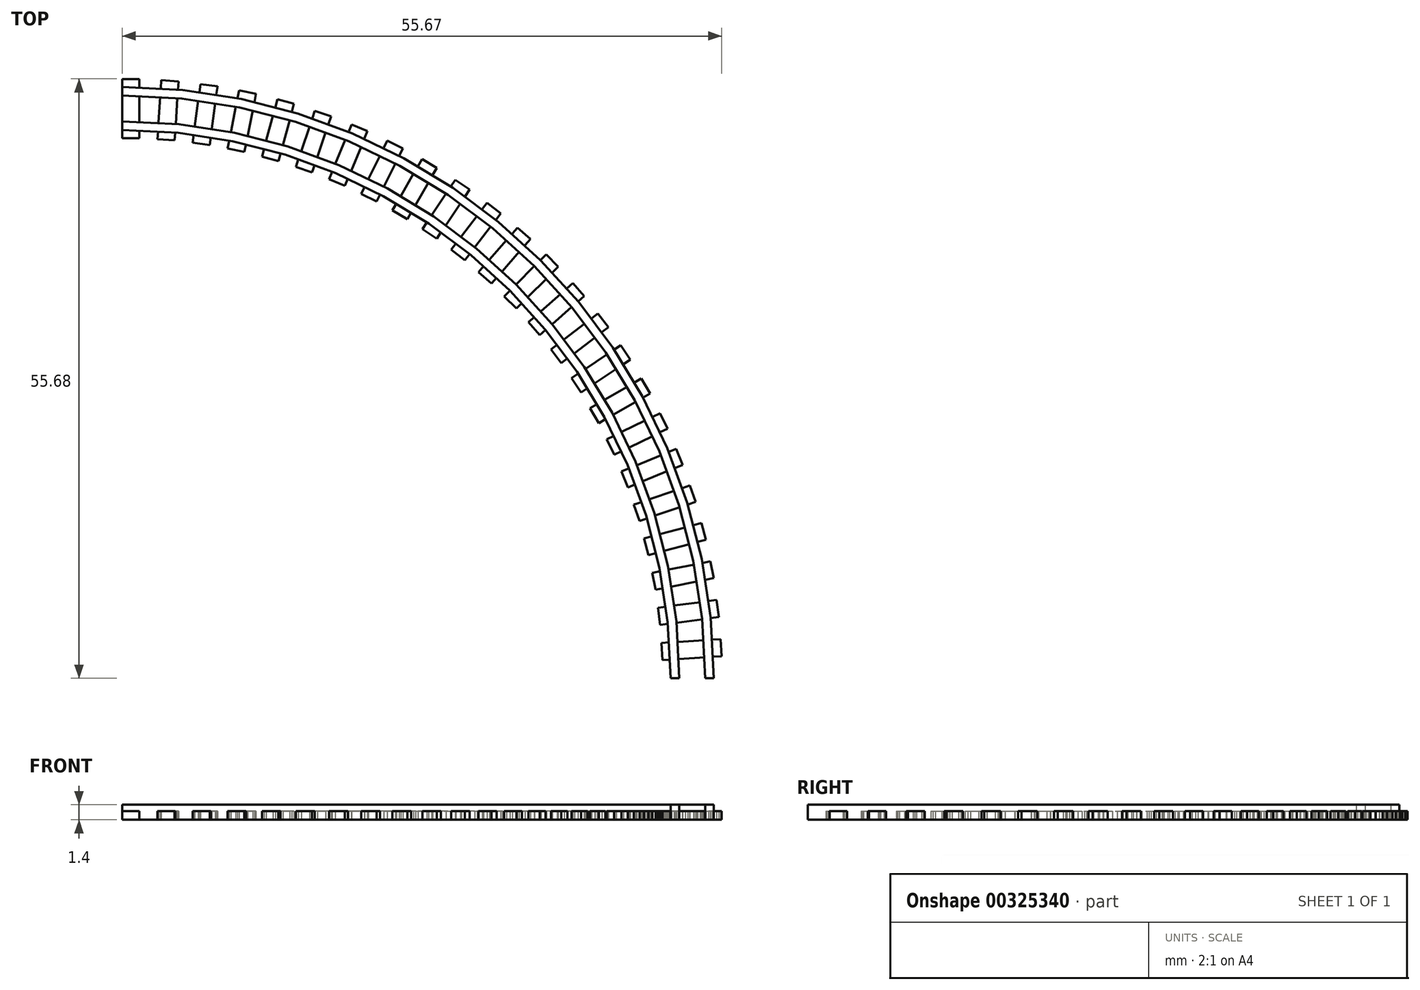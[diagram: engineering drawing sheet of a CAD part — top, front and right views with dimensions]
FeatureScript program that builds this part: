
annotation { "Feature Type Name" : "Feature", "Feature Type Description" : "" }
export const myFeature = defineFeature(function(context is Context, id is Id, definition is map)
    precondition{}
    {
        {
            var Q0;
            Q0=qCreatedBy(makeId("Top.planeOp"),FACE);
            var sketch = newSketch(context, id + "F0", { "sketchPlane" : qUnion([Q0])});
            skArc(sketch, "E0", {"start": v(50.93, 0) * mm, "mid": v(36.01, 36.01) * mm, "end": v(0, 50.93) * mm});
            skLineSegment(sketch, "E1.bottom", {"start": v(1.6, 50.18) * mm, "end": v(0, 50.18) * mm});
            skLineSegment(sketch, "E1.top", {"start": v(1.6, 55.68) * mm, "end": v(0, 55.68) * mm});
            skLineSegment(sketch, "E1.left", {"start": v(1.6, 50.18) * mm, "end": v(1.6, 55.68) * mm});
            skLineSegment(sketch, "E1.right", {"start": v(0, 50.18) * mm, "end": v(0, 55.68) * mm});
            skPoint(sketch, "E1.middle", {"position": v(0.8, 52.93) * mm});
            skLineSegment(sketch, "E2.1.0", {"start": v(4.88, 49.97) * mm, "end": v(5.24, 55.46) * mm});
            skLineSegment(sketch, "E2.1.1", {"start": v(5.24, 55.46) * mm, "end": v(3.64, 55.56) * mm});
            skLineSegment(sketch, "E2.1.2", {"start": v(3.28, 50.07) * mm, "end": v(3.64, 55.56) * mm});
            skLineSegment(sketch, "E2.1.3", {"start": v(4.88, 49.97) * mm, "end": v(3.28, 50.07) * mm});
            skLineSegment(sketch, "E2.2.0", {"start": v(8.14, 49.54) * mm, "end": v(8.85, 55) * mm});
            skLineSegment(sketch, "E2.2.1", {"start": v(8.85, 55) * mm, "end": v(7.27, 55.2) * mm});
            skLineSegment(sketch, "E2.2.2", {"start": v(6.55, 49.75) * mm, "end": v(7.27, 55.2) * mm});
            skLineSegment(sketch, "E2.2.3", {"start": v(8.14, 49.54) * mm, "end": v(6.55, 49.75) * mm});
            skLineSegment(sketch, "E2.3.0", {"start": v(11.36, 48.9) * mm, "end": v(12.43, 54.3) * mm});
            skLineSegment(sketch, "E2.3.1", {"start": v(12.43, 54.3) * mm, "end": v(10.86, 54.6) * mm});
            skLineSegment(sketch, "E2.3.2", {"start": v(9.79, 49.22) * mm, "end": v(10.86, 54.6) * mm});
            skLineSegment(sketch, "E2.3.3", {"start": v(11.36, 48.9) * mm, "end": v(9.79, 49.22) * mm});
            skLineSegment(sketch, "E2.4.0", {"start": v(14.53, 48.06) * mm, "end": v(15.96, 53.37) * mm});
            skLineSegment(sketch, "E2.4.1", {"start": v(15.96, 53.37) * mm, "end": v(14.41, 53.78) * mm});
            skLineSegment(sketch, "E2.4.2", {"start": v(12.99, 48.47) * mm, "end": v(14.41, 53.78) * mm});
            skLineSegment(sketch, "E2.4.3", {"start": v(14.53, 48.06) * mm, "end": v(12.99, 48.47) * mm});
            skLineSegment(sketch, "E2.5.0", {"start": v(17.64, 47) * mm, "end": v(19.41, 52.21) * mm});
            skLineSegment(sketch, "E2.5.1", {"start": v(19.41, 52.21) * mm, "end": v(17.9, 52.72) * mm});
            skLineSegment(sketch, "E2.5.2", {"start": v(16.13, 47.52) * mm, "end": v(17.9, 52.72) * mm});
            skLineSegment(sketch, "E2.5.3", {"start": v(17.64, 47) * mm, "end": v(16.13, 47.52) * mm});
            skLineSegment(sketch, "E2.6.0", {"start": v(20.68, 45.75) * mm, "end": v(22.79, 50.83) * mm});
            skLineSegment(sketch, "E2.6.1", {"start": v(22.79, 50.83) * mm, "end": v(21.3, 51.44) * mm});
            skLineSegment(sketch, "E2.6.2", {"start": v(19.2, 46.36) * mm, "end": v(21.3, 51.44) * mm});
            skLineSegment(sketch, "E2.6.3", {"start": v(20.68, 45.75) * mm, "end": v(19.2, 46.36) * mm});
            skLineSegment(sketch, "E2.7.0", {"start": v(23.63, 44.3) * mm, "end": v(26.06, 49.23) * mm});
            skLineSegment(sketch, "E2.7.1", {"start": v(26.06, 49.23) * mm, "end": v(24.63, 49.94) * mm});
            skLineSegment(sketch, "E2.7.2", {"start": v(22.2, 45) * mm, "end": v(24.63, 49.94) * mm});
            skLineSegment(sketch, "E2.7.3", {"start": v(23.63, 44.3) * mm, "end": v(22.2, 45) * mm});
            skLineSegment(sketch, "E2.8.0", {"start": v(26.48, 42.66) * mm, "end": v(29.23, 47.42) * mm});
            skLineSegment(sketch, "E2.8.1", {"start": v(29.23, 47.42) * mm, "end": v(27.84, 48.22) * mm});
            skLineSegment(sketch, "E2.8.2", {"start": v(25.09, 43.46) * mm, "end": v(27.84, 48.22) * mm});
            skLineSegment(sketch, "E2.8.3", {"start": v(26.48, 42.66) * mm, "end": v(25.09, 43.46) * mm});
            skLineSegment(sketch, "E2.9.0", {"start": v(29.2, 40.83) * mm, "end": v(32.26, 45.4) * mm});
            skLineSegment(sketch, "E2.9.1", {"start": v(32.26, 45.4) * mm, "end": v(30.93, 46.3) * mm});
            skLineSegment(sketch, "E2.9.2", {"start": v(27.88, 41.72) * mm, "end": v(30.93, 46.3) * mm});
            skLineSegment(sketch, "E2.9.3", {"start": v(29.2, 40.83) * mm, "end": v(27.88, 41.72) * mm});
            skLineSegment(sketch, "E2.10.0", {"start": v(31.82, 38.84) * mm, "end": v(35.16, 43.2) * mm});
            skLineSegment(sketch, "E2.10.1", {"start": v(35.16, 43.2) * mm, "end": v(33.9, 44.17) * mm});
            skLineSegment(sketch, "E2.10.2", {"start": v(30.55, 39.81) * mm, "end": v(33.9, 44.17) * mm});
            skLineSegment(sketch, "E2.10.3", {"start": v(31.82, 38.84) * mm, "end": v(30.55, 39.81) * mm});
            skLineSegment(sketch, "E2.11.0", {"start": v(34.29, 36.67) * mm, "end": v(37.92, 40.8) * mm});
            skLineSegment(sketch, "E2.11.1", {"start": v(37.92, 40.8) * mm, "end": v(36.71, 41.86) * mm});
            skLineSegment(sketch, "E2.11.2", {"start": v(33.09, 37.73) * mm, "end": v(36.71, 41.86) * mm});
            skLineSegment(sketch, "E2.11.3", {"start": v(34.29, 36.67) * mm, "end": v(33.09, 37.73) * mm});
            skLineSegment(sketch, "E2.12.0", {"start": v(36.61, 34.35) * mm, "end": v(40.5, 38.24) * mm});
            skLineSegment(sketch, "E2.12.1", {"start": v(40.5, 38.24) * mm, "end": v(39.37, 39.37) * mm});
            skLineSegment(sketch, "E2.12.2", {"start": v(35.48, 35.48) * mm, "end": v(39.37, 39.37) * mm});
            skLineSegment(sketch, "E2.12.3", {"start": v(36.61, 34.35) * mm, "end": v(35.48, 35.48) * mm});
            skLineSegment(sketch, "E2.13.0", {"start": v(38.78, 31.88) * mm, "end": v(42.92, 35.5) * mm});
            skLineSegment(sketch, "E2.13.1", {"start": v(42.92, 35.5) * mm, "end": v(41.86, 36.71) * mm});
            skLineSegment(sketch, "E2.13.2", {"start": v(37.73, 33.09) * mm, "end": v(41.86, 36.71) * mm});
            skLineSegment(sketch, "E2.13.3", {"start": v(38.78, 31.88) * mm, "end": v(37.73, 33.09) * mm});
            skLineSegment(sketch, "E2.14.0", {"start": v(40.78, 29.28) * mm, "end": v(45.15, 32.63) * mm});
            skLineSegment(sketch, "E2.14.1", {"start": v(45.15, 32.63) * mm, "end": v(44.17, 33.9) * mm});
            skLineSegment(sketch, "E2.14.2", {"start": v(39.81, 30.55) * mm, "end": v(44.17, 33.9) * mm});
            skLineSegment(sketch, "E2.14.3", {"start": v(40.78, 29.28) * mm, "end": v(39.81, 30.55) * mm});
            skLineSegment(sketch, "E2.15.0", {"start": v(42.61, 26.55) * mm, "end": v(47.18, 29.6) * mm});
            skLineSegment(sketch, "E2.15.1", {"start": v(47.18, 29.6) * mm, "end": v(46.3, 30.93) * mm});
            skLineSegment(sketch, "E2.15.2", {"start": v(41.72, 27.88) * mm, "end": v(46.3, 30.93) * mm});
            skLineSegment(sketch, "E2.15.3", {"start": v(42.61, 26.55) * mm, "end": v(41.72, 27.88) * mm});
            skLineSegment(sketch, "E2.16.0", {"start": v(44.26, 23.7) * mm, "end": v(49.02, 26.45) * mm});
            skLineSegment(sketch, "E2.16.1", {"start": v(49.02, 26.45) * mm, "end": v(48.22, 27.84) * mm});
            skLineSegment(sketch, "E2.16.2", {"start": v(43.46, 25.09) * mm, "end": v(48.22, 27.84) * mm});
            skLineSegment(sketch, "E2.16.3", {"start": v(44.26, 23.7) * mm, "end": v(43.46, 25.09) * mm});
            skLineSegment(sketch, "E2.17.0", {"start": v(45.71, 20.76) * mm, "end": v(50.65, 23.2) * mm});
            skLineSegment(sketch, "E2.17.1", {"start": v(50.65, 23.2) * mm, "end": v(49.94, 24.63) * mm});
            skLineSegment(sketch, "E2.17.2", {"start": v(45, 22.2) * mm, "end": v(49.94, 24.63) * mm});
            skLineSegment(sketch, "E2.17.3", {"start": v(45.71, 20.76) * mm, "end": v(45, 22.2) * mm});
            skLineSegment(sketch, "E2.18.0", {"start": v(46.97, 17.72) * mm, "end": v(52.05, 19.83) * mm});
            skLineSegment(sketch, "E2.18.1", {"start": v(52.05, 19.83) * mm, "end": v(51.44, 21.3) * mm});
            skLineSegment(sketch, "E2.18.2", {"start": v(46.36, 19.2) * mm, "end": v(51.44, 21.3) * mm});
            skLineSegment(sketch, "E2.18.3", {"start": v(46.97, 17.72) * mm, "end": v(46.36, 19.2) * mm});
            skLineSegment(sketch, "E2.19.0", {"start": v(48.03, 14.61) * mm, "end": v(53.24, 16.38) * mm});
            skLineSegment(sketch, "E2.19.1", {"start": v(53.24, 16.38) * mm, "end": v(52.72, 17.9) * mm});
            skLineSegment(sketch, "E2.19.2", {"start": v(47.52, 16.13) * mm, "end": v(52.72, 17.9) * mm});
            skLineSegment(sketch, "E2.19.3", {"start": v(48.03, 14.61) * mm, "end": v(47.52, 16.13) * mm});
            skLineSegment(sketch, "E2.20.0", {"start": v(48.88, 11.44) * mm, "end": v(54.2, 12.87) * mm});
            skLineSegment(sketch, "E2.20.1", {"start": v(54.2, 12.87) * mm, "end": v(53.78, 14.41) * mm});
            skLineSegment(sketch, "E2.20.2", {"start": v(48.47, 12.99) * mm, "end": v(53.78, 14.41) * mm});
            skLineSegment(sketch, "E2.20.3", {"start": v(48.88, 11.44) * mm, "end": v(48.47, 12.99) * mm});
            skLineSegment(sketch, "E2.21.0", {"start": v(49.53, 8.22) * mm, "end": v(54.92, 9.3) * mm});
            skLineSegment(sketch, "E2.21.1", {"start": v(54.92, 9.3) * mm, "end": v(54.6, 10.86) * mm});
            skLineSegment(sketch, "E2.21.2", {"start": v(49.22, 9.79) * mm, "end": v(54.6, 10.86) * mm});
            skLineSegment(sketch, "E2.21.3", {"start": v(49.53, 8.22) * mm, "end": v(49.22, 9.79) * mm});
            skLineSegment(sketch, "E2.22.0", {"start": v(49.96, 4.96) * mm, "end": v(55.41, 5.68) * mm});
            skLineSegment(sketch, "E2.22.1", {"start": v(55.41, 5.68) * mm, "end": v(55.2, 7.27) * mm});
            skLineSegment(sketch, "E2.22.2", {"start": v(49.75, 6.55) * mm, "end": v(55.2, 7.27) * mm});
            skLineSegment(sketch, "E2.22.3", {"start": v(49.96, 4.96) * mm, "end": v(49.75, 6.55) * mm});
            skLineSegment(sketch, "E2.23.0", {"start": v(50.18, 1.69) * mm, "end": v(55.67, 2.05) * mm});
            skLineSegment(sketch, "E2.23.1", {"start": v(55.67, 2.05) * mm, "end": v(55.56, 3.64) * mm});
            skLineSegment(sketch, "E2.23.2", {"start": v(50.07, 3.28) * mm, "end": v(55.56, 3.64) * mm});
            skLineSegment(sketch, "E2.23.3", {"start": v(50.18, 1.69) * mm, "end": v(50.07, 3.28) * mm});
            skLineSegment(sketch, "E3.0.24.0", {"start": v(50.18, -1.6) * mm, "end": v(55.68, -1.6) * mm});
            skLineSegment(sketch, "E3.3.24.0", {"start": v(55.68, -1.6) * mm, "end": v(55.68, 0) * mm});
            skLineSegment(sketch, "E3.6.24.0", {"start": v(50.18, 0) * mm, "end": v(55.68, 0) * mm});
            skLineSegment(sketch, "E3.9.24.0", {"start": v(50.18, -1.6) * mm, "end": v(50.18, 0) * mm});
            skArc(sketch, "E4", {"start": v(51.74, 0) * mm, "mid": v(36.59, 36.59) * mm, "end": v(0, 51.74) * mm});
            skArc(sketch, "E5", {"start": v(54.14, 0) * mm, "mid": v(38.28, 38.28) * mm, "end": v(0, 54.14) * mm});
            skArc(sketch, "E6", {"start": v(54.94, 0) * mm, "mid": v(38.85, 38.85) * mm, "end": v(0, 54.94) * mm});
            skSolve(sketch);
        }
        {
            var Q0;
            {var subQ0=sQuery(id+"F0.wireOp",EDGE,"E4");var subQ1=sQuery(id+"F0.wireOp",EDGE,"E2.5.0");var subQ2=makeQuery(id+"F0.imprint","INTERSECT",VERTEX,{"derivedFrom":[subQ1,subQ0]});Q0=makeQuery(id+"F0.imprint","IMPRINT",FACE,{"disambiguationData":[TD([[makeQuery(id+"F0.imprint","IMPRINT",EDGE,{"disambiguationData":[TD([[subQ2,-1.0]])],"derivedFrom":subQ1}),1.0]])]});}
            var Q1;
            {var subQ0=sQuery(id+"F0.wireOp",EDGE,"E2.3.0");var subQ1=sQuery(id+"F0.wireOp",EDGE,"E0");var subQ2=makeQuery(id+"F0.imprint","INTERSECT",VERTEX,{"derivedFrom":[subQ1,subQ0]});Q1=makeQuery(id+"F0.imprint","IMPRINT",FACE,{"disambiguationData":[TD([[makeQuery(id+"F0.imprint","IMPRINT",EDGE,{"disambiguationData":[TD([[subQ2,-1.0]])],"derivedFrom":subQ1}),-1.0]])]});}
            var Q2;
            {var subQ0=sQuery(id+"F0.wireOp",EDGE,"E4");var subQ1=sQuery(id+"F0.wireOp",EDGE,"E2.21.0");var subQ2=makeQuery(id+"F0.imprint","INTERSECT",VERTEX,{"derivedFrom":[subQ1,subQ0]});Q2=makeQuery(id+"F0.imprint","IMPRINT",FACE,{"disambiguationData":[TD([[makeQuery(id+"F0.imprint","IMPRINT",EDGE,{"disambiguationData":[TD([[subQ2,-1.0]])],"derivedFrom":subQ1}),1.0]])]});}
            var Q3;
            {var subQ0=sQuery(id+"F0.wireOp",EDGE,"E4");var subQ1=sQuery(id+"F0.wireOp",EDGE,"E2.3.0");var subQ2=makeQuery(id+"F0.imprint","INTERSECT",VERTEX,{"derivedFrom":[subQ1,subQ0]});Q3=makeQuery(id+"F0.imprint","IMPRINT",FACE,{"disambiguationData":[TD([[makeQuery(id+"F0.imprint","IMPRINT",EDGE,{"disambiguationData":[TD([[subQ2,-1.0]])],"derivedFrom":subQ1}),1.0]])]});}
            var Q4;
            {var subQ0=sQuery(id+"F0.wireOp",EDGE,"E4");var subQ1=sQuery(id+"F0.wireOp",EDGE,"E2.19.0");var subQ2=makeQuery(id+"F0.imprint","INTERSECT",VERTEX,{"derivedFrom":[subQ1,subQ0]});Q4=makeQuery(id+"F0.imprint","IMPRINT",FACE,{"disambiguationData":[TD([[makeQuery(id+"F0.imprint","IMPRINT",EDGE,{"disambiguationData":[TD([[subQ2,-1.0]])],"derivedFrom":subQ1}),1.0]])]});}
            var Q5;
            {var subQ0=sQuery(id+"F0.wireOp",EDGE,"E4");var subQ1=sQuery(id+"F0.wireOp",EDGE,"E2.16.0");var subQ2=makeQuery(id+"F0.imprint","INTERSECT",VERTEX,{"derivedFrom":[subQ1,subQ0]});Q5=makeQuery(id+"F0.imprint","IMPRINT",FACE,{"disambiguationData":[TD([[makeQuery(id+"F0.imprint","IMPRINT",EDGE,{"disambiguationData":[TD([[subQ2,-1.0]])],"derivedFrom":subQ1}),1.0]])]});}
            var Q6;
            {var subQ0=sQuery(id+"F0.wireOp",EDGE,"E4");var subQ1=sQuery(id+"F0.wireOp",EDGE,"E2.11.0");var subQ2=makeQuery(id+"F0.imprint","INTERSECT",VERTEX,{"derivedFrom":[subQ1,subQ0]});Q6=makeQuery(id+"F0.imprint","IMPRINT",FACE,{"disambiguationData":[TD([[makeQuery(id+"F0.imprint","IMPRINT",EDGE,{"disambiguationData":[TD([[subQ2,-1.0]])],"derivedFrom":subQ1}),1.0]])]});}
            var Q7;
            {var subQ0=sQuery(id+"F0.wireOp",EDGE,"E4");var subQ1=sQuery(id+"F0.wireOp",EDGE,"E2.22.0");var subQ2=makeQuery(id+"F0.imprint","INTERSECT",VERTEX,{"derivedFrom":[subQ1,subQ0]});Q7=makeQuery(id+"F0.imprint","IMPRINT",FACE,{"disambiguationData":[TD([[makeQuery(id+"F0.imprint","IMPRINT",EDGE,{"disambiguationData":[TD([[subQ2,-1.0]])],"derivedFrom":subQ1}),1.0]])]});}
            var Q8;
            {var subQ0=sQuery(id+"F0.wireOp",EDGE,"E4");var subQ1=sQuery(id+"F0.wireOp",EDGE,"E2.7.0");var subQ2=makeQuery(id+"F0.imprint","INTERSECT",VERTEX,{"derivedFrom":[subQ1,subQ0]});Q8=makeQuery(id+"F0.imprint","IMPRINT",FACE,{"disambiguationData":[TD([[makeQuery(id+"F0.imprint","IMPRINT",EDGE,{"disambiguationData":[TD([[subQ2,-1.0]])],"derivedFrom":subQ1}),1.0]])]});}
            var Q9;
            {var subQ0=sQuery(id+"F0.wireOp",EDGE,"E4");var subQ1=sQuery(id+"F0.wireOp",EDGE,"E2.4.0");var subQ2=makeQuery(id+"F0.imprint","INTERSECT",VERTEX,{"derivedFrom":[subQ1,subQ0]});Q9=makeQuery(id+"F0.imprint","IMPRINT",FACE,{"disambiguationData":[TD([[makeQuery(id+"F0.imprint","IMPRINT",EDGE,{"disambiguationData":[TD([[subQ2,-1.0]])],"derivedFrom":subQ1}),1.0]])]});}
            var Q10;
            {var subQ0=sQuery(id+"F0.wireOp",EDGE,"E4");var subQ1=sQuery(id+"F0.wireOp",EDGE,"E2.1.0");var subQ2=makeQuery(id+"F0.imprint","INTERSECT",VERTEX,{"derivedFrom":[subQ1,subQ0]});Q10=makeQuery(id+"F0.imprint","IMPRINT",FACE,{"disambiguationData":[TD([[makeQuery(id+"F0.imprint","IMPRINT",EDGE,{"disambiguationData":[TD([[subQ2,-1.0]])],"derivedFrom":subQ1}),1.0]])]});}
            var Q11;
            {var subQ0=sQuery(id+"F0.wireOp",EDGE,"E4");var subQ1=sQuery(id+"F0.wireOp",EDGE,"E2.17.0");var subQ2=makeQuery(id+"F0.imprint","INTERSECT",VERTEX,{"derivedFrom":[subQ1,subQ0]});Q11=makeQuery(id+"F0.imprint","IMPRINT",FACE,{"disambiguationData":[TD([[makeQuery(id+"F0.imprint","IMPRINT",EDGE,{"disambiguationData":[TD([[subQ2,-1.0]])],"derivedFrom":subQ1}),1.0]])]});}
            var Q12;
            {var subQ0=sQuery(id+"F0.wireOp",EDGE,"E4");var subQ1=sQuery(id+"F0.wireOp",EDGE,"E2.10.0");var subQ2=makeQuery(id+"F0.imprint","INTERSECT",VERTEX,{"derivedFrom":[subQ1,subQ0]});Q12=makeQuery(id+"F0.imprint","IMPRINT",FACE,{"disambiguationData":[TD([[makeQuery(id+"F0.imprint","IMPRINT",EDGE,{"disambiguationData":[TD([[subQ2,-1.0]])],"derivedFrom":subQ1}),1.0]])]});}
            var Q13;
            {var subQ0=sQuery(id+"F0.wireOp",EDGE,"E4");var subQ1=sQuery(id+"F0.wireOp",EDGE,"E2.13.0");var subQ2=makeQuery(id+"F0.imprint","INTERSECT",VERTEX,{"derivedFrom":[subQ1,subQ0]});Q13=makeQuery(id+"F0.imprint","IMPRINT",FACE,{"disambiguationData":[TD([[makeQuery(id+"F0.imprint","IMPRINT",EDGE,{"disambiguationData":[TD([[subQ2,-1.0]])],"derivedFrom":subQ1}),1.0]])]});}
            var Q14;
            {var subQ0=sQuery(id+"F0.wireOp",EDGE,"E4");var subQ1=sQuery(id+"F0.wireOp",EDGE,"E2.8.0");var subQ2=makeQuery(id+"F0.imprint","INTERSECT",VERTEX,{"derivedFrom":[subQ1,subQ0]});Q14=makeQuery(id+"F0.imprint","IMPRINT",FACE,{"disambiguationData":[TD([[makeQuery(id+"F0.imprint","IMPRINT",EDGE,{"disambiguationData":[TD([[subQ2,-1.0]])],"derivedFrom":subQ1}),1.0]])]});}
            var Q15;
            {var subQ0=sQuery(id+"F0.wireOp",EDGE,"E4");var subQ1=sQuery(id+"F0.wireOp",EDGE,"E2.15.0");var subQ2=makeQuery(id+"F0.imprint","INTERSECT",VERTEX,{"derivedFrom":[subQ1,subQ0]});Q15=makeQuery(id+"F0.imprint","IMPRINT",FACE,{"disambiguationData":[TD([[makeQuery(id+"F0.imprint","IMPRINT",EDGE,{"disambiguationData":[TD([[subQ2,-1.0]])],"derivedFrom":subQ1}),1.0]])]});}
            var Q16;
            {var subQ0=sQuery(id+"F0.wireOp",EDGE,"E4");var subQ1=sQuery(id+"F0.wireOp",EDGE,"E2.2.0");var subQ2=makeQuery(id+"F0.imprint","INTERSECT",VERTEX,{"derivedFrom":[subQ1,subQ0]});Q16=makeQuery(id+"F0.imprint","IMPRINT",FACE,{"disambiguationData":[TD([[makeQuery(id+"F0.imprint","IMPRINT",EDGE,{"disambiguationData":[TD([[subQ2,-1.0]])],"derivedFrom":subQ1}),1.0]])]});}
            var Q17;
            {var subQ0=sQuery(id+"F0.wireOp",EDGE,"E4");var subQ1=sQuery(id+"F0.wireOp",EDGE,"E2.18.0");var subQ2=makeQuery(id+"F0.imprint","INTERSECT",VERTEX,{"derivedFrom":[subQ1,subQ0]});Q17=makeQuery(id+"F0.imprint","IMPRINT",FACE,{"disambiguationData":[TD([[makeQuery(id+"F0.imprint","IMPRINT",EDGE,{"disambiguationData":[TD([[subQ2,-1.0]])],"derivedFrom":subQ1}),1.0]])]});}
            var Q18;
            {var subQ0=sQuery(id+"F0.wireOp",EDGE,"E4");var subQ1=sQuery(id+"F0.wireOp",EDGE,"E2.20.0");var subQ2=makeQuery(id+"F0.imprint","INTERSECT",VERTEX,{"derivedFrom":[subQ1,subQ0]});Q18=makeQuery(id+"F0.imprint","IMPRINT",FACE,{"disambiguationData":[TD([[makeQuery(id+"F0.imprint","IMPRINT",EDGE,{"disambiguationData":[TD([[subQ2,-1.0]])],"derivedFrom":subQ1}),1.0]])]});}
            var Q19;
            {var subQ0=sQuery(id+"F0.wireOp",EDGE,"E4");var subQ1=sQuery(id+"F0.wireOp",EDGE,"E2.23.0");var subQ2=makeQuery(id+"F0.imprint","INTERSECT",VERTEX,{"derivedFrom":[subQ1,subQ0]});Q19=makeQuery(id+"F0.imprint","IMPRINT",FACE,{"disambiguationData":[TD([[makeQuery(id+"F0.imprint","IMPRINT",EDGE,{"disambiguationData":[TD([[subQ2,-1.0]])],"derivedFrom":subQ1}),1.0]])]});}
            var Q20;
            {var subQ0=sQuery(id+"F0.wireOp",EDGE,"E4");var subQ1=sQuery(id+"F0.wireOp",EDGE,"E2.6.0");var subQ2=makeQuery(id+"F0.imprint","INTERSECT",VERTEX,{"derivedFrom":[subQ1,subQ0]});Q20=makeQuery(id+"F0.imprint","IMPRINT",FACE,{"disambiguationData":[TD([[makeQuery(id+"F0.imprint","IMPRINT",EDGE,{"disambiguationData":[TD([[subQ2,-1.0]])],"derivedFrom":subQ1}),1.0]])]});}
            var Q21;
            {var subQ0=sQuery(id+"F0.wireOp",EDGE,"E4");var subQ1=sQuery(id+"F0.wireOp",EDGE,"E2.12.0");var subQ2=makeQuery(id+"F0.imprint","INTERSECT",VERTEX,{"derivedFrom":[subQ1,subQ0]});Q21=makeQuery(id+"F0.imprint","IMPRINT",FACE,{"disambiguationData":[TD([[makeQuery(id+"F0.imprint","IMPRINT",EDGE,{"disambiguationData":[TD([[subQ2,-1.0]])],"derivedFrom":subQ1}),1.0]])]});}
            var Q22;
            {var subQ0=sQuery(id+"F0.wireOp",EDGE,"E4");var subQ1=sQuery(id+"F0.wireOp",EDGE,"E2.9.0");var subQ2=makeQuery(id+"F0.imprint","INTERSECT",VERTEX,{"derivedFrom":[subQ1,subQ0]});Q22=makeQuery(id+"F0.imprint","IMPRINT",FACE,{"disambiguationData":[TD([[makeQuery(id+"F0.imprint","IMPRINT",EDGE,{"disambiguationData":[TD([[subQ2,-1.0]])],"derivedFrom":subQ1}),1.0]])]});}
            var Q23;
            {var subQ0=sQuery(id+"F0.wireOp",EDGE,"E4");var subQ1=sQuery(id+"F0.wireOp",EDGE,"E2.14.0");var subQ2=makeQuery(id+"F0.imprint","INTERSECT",VERTEX,{"derivedFrom":[subQ1,subQ0]});Q23=makeQuery(id+"F0.imprint","IMPRINT",FACE,{"disambiguationData":[TD([[makeQuery(id+"F0.imprint","IMPRINT",EDGE,{"disambiguationData":[TD([[subQ2,-1.0]])],"derivedFrom":subQ1}),1.0]])]});}
            var Q24;
            {var subQ0=sQuery(id+"F0.wireOp",EDGE,"E2.6.2");var subQ1=sQuery(id+"F0.wireOp",EDGE,"E0");var subQ2=makeQuery(id+"F0.imprint","INTERSECT",VERTEX,{"derivedFrom":[subQ1,subQ0]});Q24=makeQuery(id+"F0.imprint","IMPRINT",FACE,{"disambiguationData":[TD([[makeQuery(id+"F0.imprint","IMPRINT",EDGE,{"disambiguationData":[TD([[subQ2,-1.0]])],"derivedFrom":subQ1}),-1.0]])]});}
            var Q25;
            {var subQ0=sQuery(id+"F0.wireOp",EDGE,"E2.10.0");var subQ1=sQuery(id+"F0.wireOp",EDGE,"E0");var subQ2=makeQuery(id+"F0.imprint","INTERSECT",VERTEX,{"derivedFrom":[subQ1,subQ0]});Q25=makeQuery(id+"F0.imprint","IMPRINT",FACE,{"disambiguationData":[TD([[makeQuery(id+"F0.imprint","IMPRINT",EDGE,{"disambiguationData":[TD([[subQ2,-1.0]])],"derivedFrom":subQ1}),-1.0]])]});}
            var Q26;
            {var subQ0=sQuery(id+"F0.wireOp",EDGE,"E6");var subQ1=sQuery(id+"F0.wireOp",EDGE,"E2.21.0");var subQ2=makeQuery(id+"F0.imprint","INTERSECT",VERTEX,{"derivedFrom":[subQ1,subQ0]});Q26=makeQuery(id+"F0.imprint","IMPRINT",FACE,{"disambiguationData":[TD([[makeQuery(id+"F0.imprint","IMPRINT",EDGE,{"disambiguationData":[TD([[subQ2,1.0]])],"derivedFrom":subQ1}),-1.0]])]});}
            var Q27;
            {var subQ0=sQuery(id+"F0.wireOp",EDGE,"E6");var subQ1=sQuery(id+"F0.wireOp",EDGE,"E2.22.0");var subQ2=makeQuery(id+"F0.imprint","INTERSECT",VERTEX,{"derivedFrom":[subQ1,subQ0]});Q27=makeQuery(id+"F0.imprint","IMPRINT",FACE,{"disambiguationData":[TD([[makeQuery(id+"F0.imprint","IMPRINT",EDGE,{"disambiguationData":[TD([[subQ2,1.0]])],"derivedFrom":subQ1}),-1.0]])]});}
            var Q28;
            {var subQ0=sQuery(id+"F0.wireOp",EDGE,"E2.4.0");var subQ1=sQuery(id+"F0.wireOp",EDGE,"E0");var subQ2=makeQuery(id+"F0.imprint","INTERSECT",VERTEX,{"derivedFrom":[subQ1,subQ0]});Q28=makeQuery(id+"F0.imprint","IMPRINT",FACE,{"disambiguationData":[TD([[makeQuery(id+"F0.imprint","IMPRINT",EDGE,{"disambiguationData":[TD([[subQ2,-1.0]])],"derivedFrom":subQ1}),-1.0]])]});}
            var Q29;
            {var subQ0=sQuery(id+"F0.wireOp",EDGE,"E2.16.2");var subQ1=sQuery(id+"F0.wireOp",EDGE,"E0");var subQ2=makeQuery(id+"F0.imprint","INTERSECT",VERTEX,{"derivedFrom":[subQ1,subQ0]});Q29=makeQuery(id+"F0.imprint","IMPRINT",FACE,{"disambiguationData":[TD([[makeQuery(id+"F0.imprint","IMPRINT",EDGE,{"disambiguationData":[TD([[subQ2,-1.0]])],"derivedFrom":subQ1}),-1.0]])]});}
            var Q30;
            {var subQ0=sQuery(id+"F0.wireOp",EDGE,"E6");var subQ1=sQuery(id+"F0.wireOp",EDGE,"E2.13.0");var subQ2=makeQuery(id+"F0.imprint","INTERSECT",VERTEX,{"derivedFrom":[subQ1,subQ0]});Q30=makeQuery(id+"F0.imprint","IMPRINT",FACE,{"disambiguationData":[TD([[makeQuery(id+"F0.imprint","IMPRINT",EDGE,{"disambiguationData":[TD([[subQ2,1.0]])],"derivedFrom":subQ1}),-1.0]])]});}
            var Q31;
            {var subQ0=sQuery(id+"F0.wireOp",EDGE,"E6");var subQ1=sQuery(id+"F0.wireOp",EDGE,"E2.20.0");var subQ2=makeQuery(id+"F0.imprint","INTERSECT",VERTEX,{"derivedFrom":[subQ1,subQ0]});Q31=makeQuery(id+"F0.imprint","IMPRINT",FACE,{"disambiguationData":[TD([[makeQuery(id+"F0.imprint","IMPRINT",EDGE,{"disambiguationData":[TD([[subQ2,1.0]])],"derivedFrom":subQ1}),-1.0]])]});}
            var Q32;
            {var subQ0=sQuery(id+"F0.wireOp",EDGE,"E6");var subQ1=sQuery(id+"F0.wireOp",EDGE,"E2.4.0");var subQ2=makeQuery(id+"F0.imprint","INTERSECT",VERTEX,{"derivedFrom":[subQ1,subQ0]});Q32=makeQuery(id+"F0.imprint","IMPRINT",FACE,{"disambiguationData":[TD([[makeQuery(id+"F0.imprint","IMPRINT",EDGE,{"disambiguationData":[TD([[subQ2,1.0]])],"derivedFrom":subQ1}),-1.0]])]});}
            var Q33;
            {var subQ0=sQuery(id+"F0.wireOp",EDGE,"E6");var subQ1=sQuery(id+"F0.wireOp",EDGE,"E2.21.0");var subQ2=makeQuery(id+"F0.imprint","INTERSECT",VERTEX,{"derivedFrom":[subQ1,subQ0]});Q33=makeQuery(id+"F0.imprint","IMPRINT",FACE,{"disambiguationData":[TD([[makeQuery(id+"F0.imprint","IMPRINT",EDGE,{"disambiguationData":[TD([[subQ2,1.0]])],"derivedFrom":subQ1}),1.0]])]});}
            var Q34;
            {var subQ0=sQuery(id+"F0.wireOp",EDGE,"E6");var subQ1=sQuery(id+"F0.wireOp",EDGE,"E2.5.0");var subQ2=makeQuery(id+"F0.imprint","INTERSECT",VERTEX,{"derivedFrom":[subQ1,subQ0]});Q34=makeQuery(id+"F0.imprint","IMPRINT",FACE,{"disambiguationData":[TD([[makeQuery(id+"F0.imprint","IMPRINT",EDGE,{"disambiguationData":[TD([[subQ2,1.0]])],"derivedFrom":subQ1}),1.0]])]});}
            var Q35;
            {var subQ0=sQuery(id+"F0.wireOp",EDGE,"E2.4.2");var subQ1=sQuery(id+"F0.wireOp",EDGE,"E0");var subQ2=makeQuery(id+"F0.imprint","INTERSECT",VERTEX,{"derivedFrom":[subQ1,subQ0]});Q35=makeQuery(id+"F0.imprint","IMPRINT",FACE,{"disambiguationData":[TD([[makeQuery(id+"F0.imprint","IMPRINT",EDGE,{"disambiguationData":[TD([[subQ2,-1.0]])],"derivedFrom":subQ1}),-1.0]])]});}
            var Q36;
            {var subQ0=sQuery(id+"F0.wireOp",EDGE,"E6");var subQ1=sQuery(id+"F0.wireOp",EDGE,"E2.2.0");var subQ2=makeQuery(id+"F0.imprint","INTERSECT",VERTEX,{"derivedFrom":[subQ1,subQ0]});Q36=makeQuery(id+"F0.imprint","IMPRINT",FACE,{"disambiguationData":[TD([[makeQuery(id+"F0.imprint","IMPRINT",EDGE,{"disambiguationData":[TD([[subQ2,1.0]])],"derivedFrom":subQ1}),-1.0]])]});}
            var Q37;
            {var subQ0=sQuery(id+"F0.wireOp",EDGE,"E2.7.0");var subQ1=sQuery(id+"F0.wireOp",EDGE,"E0");var subQ2=makeQuery(id+"F0.imprint","INTERSECT",VERTEX,{"derivedFrom":[subQ1,subQ0]});Q37=makeQuery(id+"F0.imprint","IMPRINT",FACE,{"disambiguationData":[TD([[makeQuery(id+"F0.imprint","IMPRINT",EDGE,{"disambiguationData":[TD([[subQ2,-1.0]])],"derivedFrom":subQ1}),-1.0]])]});}
            var Q38;
            {var subQ0=sQuery(id+"F0.wireOp",EDGE,"E6");var subQ1=sQuery(id+"F0.wireOp",EDGE,"E1.left");var subQ2=makeQuery(id+"F0.imprint","INTERSECT",VERTEX,{"derivedFrom":[subQ1,subQ0]});Q38=makeQuery(id+"F0.imprint","IMPRINT",FACE,{"disambiguationData":[TD([[makeQuery(id+"F0.imprint","IMPRINT",EDGE,{"disambiguationData":[TD([[subQ2,1.0]])],"derivedFrom":subQ1}),-1.0]])]});}
            var Q39;
            {var subQ0=sQuery(id+"F0.wireOp",EDGE,"E2.10.2");var subQ1=sQuery(id+"F0.wireOp",EDGE,"E0");var subQ2=makeQuery(id+"F0.imprint","INTERSECT",VERTEX,{"derivedFrom":[subQ1,subQ0]});Q39=makeQuery(id+"F0.imprint","IMPRINT",FACE,{"disambiguationData":[TD([[makeQuery(id+"F0.imprint","IMPRINT",EDGE,{"disambiguationData":[TD([[subQ2,-1.0]])],"derivedFrom":subQ1}),-1.0]])]});}
            var Q40;
            {var subQ0=sQuery(id+"F0.wireOp",EDGE,"E2.3.2");var subQ1=sQuery(id+"F0.wireOp",EDGE,"E0");var subQ2=makeQuery(id+"F0.imprint","INTERSECT",VERTEX,{"derivedFrom":[subQ1,subQ0]});Q40=makeQuery(id+"F0.imprint","IMPRINT",FACE,{"disambiguationData":[TD([[makeQuery(id+"F0.imprint","IMPRINT",EDGE,{"disambiguationData":[TD([[subQ2,-1.0]])],"derivedFrom":subQ1}),-1.0]])]});}
            var Q41;
            {var subQ0=sQuery(id+"F0.wireOp",EDGE,"E2.19.2");var subQ1=sQuery(id+"F0.wireOp",EDGE,"E0");var subQ2=makeQuery(id+"F0.imprint","INTERSECT",VERTEX,{"derivedFrom":[subQ1,subQ0]});Q41=makeQuery(id+"F0.imprint","IMPRINT",FACE,{"disambiguationData":[TD([[makeQuery(id+"F0.imprint","IMPRINT",EDGE,{"disambiguationData":[TD([[subQ2,-1.0]])],"derivedFrom":subQ1}),-1.0]])]});}
            var Q42;
            {var subQ0=sQuery(id+"F0.wireOp",EDGE,"E2.6.0");var subQ1=sQuery(id+"F0.wireOp",EDGE,"E0");var subQ2=makeQuery(id+"F0.imprint","INTERSECT",VERTEX,{"derivedFrom":[subQ1,subQ0]});Q42=makeQuery(id+"F0.imprint","IMPRINT",FACE,{"disambiguationData":[TD([[makeQuery(id+"F0.imprint","IMPRINT",EDGE,{"disambiguationData":[TD([[subQ2,-1.0]])],"derivedFrom":subQ1}),-1.0]])]});}
            var Q43;
            {var subQ0=sQuery(id+"F0.wireOp",EDGE,"E6");var subQ1=sQuery(id+"F0.wireOp",EDGE,"E2.19.0");var subQ2=makeQuery(id+"F0.imprint","INTERSECT",VERTEX,{"derivedFrom":[subQ1,subQ0]});Q43=makeQuery(id+"F0.imprint","IMPRINT",FACE,{"disambiguationData":[TD([[makeQuery(id+"F0.imprint","IMPRINT",EDGE,{"disambiguationData":[TD([[subQ2,1.0]])],"derivedFrom":subQ1}),-1.0]])]});}
            var Q44;
            {var subQ0=sQuery(id+"F0.wireOp",EDGE,"E2.22.0");var subQ1=sQuery(id+"F0.wireOp",EDGE,"E0");var subQ2=makeQuery(id+"F0.imprint","INTERSECT",VERTEX,{"derivedFrom":[subQ1,subQ0]});Q44=makeQuery(id+"F0.imprint","IMPRINT",FACE,{"disambiguationData":[TD([[makeQuery(id+"F0.imprint","IMPRINT",EDGE,{"disambiguationData":[TD([[subQ2,-1.0]])],"derivedFrom":subQ1}),-1.0]])]});}
            var Q45;
            {var subQ0=sQuery(id+"F0.wireOp",EDGE,"E6");var subQ1=sQuery(id+"F0.wireOp",EDGE,"E2.11.0");var subQ2=makeQuery(id+"F0.imprint","INTERSECT",VERTEX,{"derivedFrom":[subQ1,subQ0]});Q45=makeQuery(id+"F0.imprint","IMPRINT",FACE,{"disambiguationData":[TD([[makeQuery(id+"F0.imprint","IMPRINT",EDGE,{"disambiguationData":[TD([[subQ2,1.0]])],"derivedFrom":subQ1}),-1.0]])]});}
            var Q46;
            {var subQ0=sQuery(id+"F0.wireOp",EDGE,"E2.2.2");var subQ1=sQuery(id+"F0.wireOp",EDGE,"E0");var subQ2=makeQuery(id+"F0.imprint","INTERSECT",VERTEX,{"derivedFrom":[subQ1,subQ0]});Q46=makeQuery(id+"F0.imprint","IMPRINT",FACE,{"disambiguationData":[TD([[makeQuery(id+"F0.imprint","IMPRINT",EDGE,{"disambiguationData":[TD([[subQ2,-1.0]])],"derivedFrom":subQ1}),-1.0]])]});}
            var Q47;
            {var subQ0=sQuery(id+"F0.wireOp",EDGE,"E2.18.2");var subQ1=sQuery(id+"F0.wireOp",EDGE,"E0");var subQ2=makeQuery(id+"F0.imprint","INTERSECT",VERTEX,{"derivedFrom":[subQ1,subQ0]});Q47=makeQuery(id+"F0.imprint","IMPRINT",FACE,{"disambiguationData":[TD([[makeQuery(id+"F0.imprint","IMPRINT",EDGE,{"disambiguationData":[TD([[subQ2,-1.0]])],"derivedFrom":subQ1}),-1.0]])]});}
            var Q48;
            {var subQ0=sQuery(id+"F0.wireOp",EDGE,"E6");var subQ1=sQuery(id+"F0.wireOp",EDGE,"E2.20.0");var subQ2=makeQuery(id+"F0.imprint","INTERSECT",VERTEX,{"derivedFrom":[subQ1,subQ0]});Q48=makeQuery(id+"F0.imprint","IMPRINT",FACE,{"disambiguationData":[TD([[makeQuery(id+"F0.imprint","IMPRINT",EDGE,{"disambiguationData":[TD([[subQ2,1.0]])],"derivedFrom":subQ1}),1.0]])]});}
            var Q49;
            {var subQ0=sQuery(id+"F0.wireOp",EDGE,"E6");var subQ1=sQuery(id+"F0.wireOp",EDGE,"E2.4.0");var subQ2=makeQuery(id+"F0.imprint","INTERSECT",VERTEX,{"derivedFrom":[subQ1,subQ0]});Q49=makeQuery(id+"F0.imprint","IMPRINT",FACE,{"disambiguationData":[TD([[makeQuery(id+"F0.imprint","IMPRINT",EDGE,{"disambiguationData":[TD([[subQ2,1.0]])],"derivedFrom":subQ1}),1.0]])]});}
            var Q50;
            {var subQ0=sQuery(id+"F0.wireOp",EDGE,"E2.11.0");var subQ1=sQuery(id+"F0.wireOp",EDGE,"E0");var subQ2=makeQuery(id+"F0.imprint","INTERSECT",VERTEX,{"derivedFrom":[subQ1,subQ0]});Q50=makeQuery(id+"F0.imprint","IMPRINT",FACE,{"disambiguationData":[TD([[makeQuery(id+"F0.imprint","IMPRINT",EDGE,{"disambiguationData":[TD([[subQ2,-1.0]])],"derivedFrom":subQ1}),-1.0]])]});}
            var Q51;
            {var subQ0=sQuery(id+"F0.wireOp",EDGE,"E6");var subQ1=sQuery(id+"F0.wireOp",EDGE,"E2.23.0");var subQ2=makeQuery(id+"F0.imprint","INTERSECT",VERTEX,{"derivedFrom":[subQ1,subQ0]});Q51=makeQuery(id+"F0.imprint","IMPRINT",FACE,{"disambiguationData":[TD([[makeQuery(id+"F0.imprint","IMPRINT",EDGE,{"disambiguationData":[TD([[subQ2,1.0]])],"derivedFrom":subQ1}),1.0]])]});}
            var Q52;
            {var subQ0=sQuery(id+"F0.wireOp",EDGE,"E2.5.0");var subQ1=sQuery(id+"F0.wireOp",EDGE,"E0");var subQ2=makeQuery(id+"F0.imprint","INTERSECT",VERTEX,{"derivedFrom":[subQ1,subQ0]});Q52=makeQuery(id+"F0.imprint","IMPRINT",FACE,{"disambiguationData":[TD([[makeQuery(id+"F0.imprint","IMPRINT",EDGE,{"disambiguationData":[TD([[subQ2,-1.0]])],"derivedFrom":subQ1}),-1.0]])]});}
            var Q53;
            {var subQ0=sQuery(id+"F0.wireOp",EDGE,"E2.9.0");var subQ1=sQuery(id+"F0.wireOp",EDGE,"E0");var subQ2=makeQuery(id+"F0.imprint","INTERSECT",VERTEX,{"derivedFrom":[subQ1,subQ0]});Q53=makeQuery(id+"F0.imprint","IMPRINT",FACE,{"disambiguationData":[TD([[makeQuery(id+"F0.imprint","IMPRINT",EDGE,{"disambiguationData":[TD([[subQ2,-1.0]])],"derivedFrom":subQ1}),-1.0]])]});}
            var Q54;
            {var subQ0=sQuery(id+"F0.wireOp",EDGE,"E6");var subQ1=sQuery(id+"F0.wireOp",EDGE,"E2.13.0");var subQ2=makeQuery(id+"F0.imprint","INTERSECT",VERTEX,{"derivedFrom":[subQ1,subQ0]});Q54=makeQuery(id+"F0.imprint","IMPRINT",FACE,{"disambiguationData":[TD([[makeQuery(id+"F0.imprint","IMPRINT",EDGE,{"disambiguationData":[TD([[subQ2,1.0]])],"derivedFrom":subQ1}),1.0]])]});}
            var Q55;
            {var subQ0=sQuery(id+"F0.wireOp",EDGE,"E2.18.0");var subQ1=sQuery(id+"F0.wireOp",EDGE,"E0");var subQ2=makeQuery(id+"F0.imprint","INTERSECT",VERTEX,{"derivedFrom":[subQ1,subQ0]});Q55=makeQuery(id+"F0.imprint","IMPRINT",FACE,{"disambiguationData":[TD([[makeQuery(id+"F0.imprint","IMPRINT",EDGE,{"disambiguationData":[TD([[subQ2,-1.0]])],"derivedFrom":subQ1}),-1.0]])]});}
            var Q56;
            {var subQ0=sQuery(id+"F0.wireOp",EDGE,"E6");var subQ1=sQuery(id+"F0.wireOp",EDGE,"E2.12.0");var subQ2=makeQuery(id+"F0.imprint","INTERSECT",VERTEX,{"derivedFrom":[subQ1,subQ0]});Q56=makeQuery(id+"F0.imprint","IMPRINT",FACE,{"disambiguationData":[TD([[makeQuery(id+"F0.imprint","IMPRINT",EDGE,{"disambiguationData":[TD([[subQ2,1.0]])],"derivedFrom":subQ1}),1.0]])]});}
            var Q57;
            {var subQ0=sQuery(id+"F0.wireOp",EDGE,"E2.15.0");var subQ1=sQuery(id+"F0.wireOp",EDGE,"E0");var subQ2=makeQuery(id+"F0.imprint","INTERSECT",VERTEX,{"derivedFrom":[subQ1,subQ0]});Q57=makeQuery(id+"F0.imprint","IMPRINT",FACE,{"disambiguationData":[TD([[makeQuery(id+"F0.imprint","IMPRINT",EDGE,{"disambiguationData":[TD([[subQ2,-1.0]])],"derivedFrom":subQ1}),-1.0]])]});}
            var Q58;
            {var subQ0=sQuery(id+"F0.wireOp",EDGE,"E6");var subQ1=sQuery(id+"F0.wireOp",EDGE,"E2.14.0");var subQ2=makeQuery(id+"F0.imprint","INTERSECT",VERTEX,{"derivedFrom":[subQ1,subQ0]});Q58=makeQuery(id+"F0.imprint","IMPRINT",FACE,{"disambiguationData":[TD([[makeQuery(id+"F0.imprint","IMPRINT",EDGE,{"disambiguationData":[TD([[subQ2,1.0]])],"derivedFrom":subQ1}),1.0]])]});}
            var Q59;
            {var subQ0=sQuery(id+"F0.wireOp",EDGE,"E6");var subQ1=sQuery(id+"F0.wireOp",EDGE,"E2.1.0");var subQ2=makeQuery(id+"F0.imprint","INTERSECT",VERTEX,{"derivedFrom":[subQ1,subQ0]});Q59=makeQuery(id+"F0.imprint","IMPRINT",FACE,{"disambiguationData":[TD([[makeQuery(id+"F0.imprint","IMPRINT",EDGE,{"disambiguationData":[TD([[subQ2,1.0]])],"derivedFrom":subQ1}),1.0]])]});}
            var Q60;
            {var subQ0=sQuery(id+"F0.wireOp",EDGE,"E2.13.2");var subQ1=sQuery(id+"F0.wireOp",EDGE,"E0");var subQ2=makeQuery(id+"F0.imprint","INTERSECT",VERTEX,{"derivedFrom":[subQ1,subQ0]});Q60=makeQuery(id+"F0.imprint","IMPRINT",FACE,{"disambiguationData":[TD([[makeQuery(id+"F0.imprint","IMPRINT",EDGE,{"disambiguationData":[TD([[subQ2,-1.0]])],"derivedFrom":subQ1}),-1.0]])]});}
            var Q61;
            {var subQ0=sQuery(id+"F0.wireOp",EDGE,"E6");var subQ1=sQuery(id+"F0.wireOp",EDGE,"E2.19.0");var subQ2=makeQuery(id+"F0.imprint","INTERSECT",VERTEX,{"derivedFrom":[subQ1,subQ0]});Q61=makeQuery(id+"F0.imprint","IMPRINT",FACE,{"disambiguationData":[TD([[makeQuery(id+"F0.imprint","IMPRINT",EDGE,{"disambiguationData":[TD([[subQ2,1.0]])],"derivedFrom":subQ1}),1.0]])]});}
            var Q62;
            {var subQ0=sQuery(id+"F0.wireOp",EDGE,"E6");var subQ1=sQuery(id+"F0.wireOp",EDGE,"E2.22.0");var subQ2=makeQuery(id+"F0.imprint","INTERSECT",VERTEX,{"derivedFrom":[subQ1,subQ0]});Q62=makeQuery(id+"F0.imprint","IMPRINT",FACE,{"disambiguationData":[TD([[makeQuery(id+"F0.imprint","IMPRINT",EDGE,{"disambiguationData":[TD([[subQ2,1.0]])],"derivedFrom":subQ1}),1.0]])]});}
            var Q63;
            {var subQ0=sQuery(id+"F0.wireOp",EDGE,"E2.20.2");var subQ1=sQuery(id+"F0.wireOp",EDGE,"E0");var subQ2=makeQuery(id+"F0.imprint","INTERSECT",VERTEX,{"derivedFrom":[subQ1,subQ0]});Q63=makeQuery(id+"F0.imprint","IMPRINT",FACE,{"disambiguationData":[TD([[makeQuery(id+"F0.imprint","IMPRINT",EDGE,{"disambiguationData":[TD([[subQ2,-1.0]])],"derivedFrom":subQ1}),-1.0]])]});}
            var Q64;
            {var subQ0=sQuery(id+"F0.wireOp",EDGE,"E6");var subQ1=sQuery(id+"F0.wireOp",EDGE,"E2.9.0");var subQ2=makeQuery(id+"F0.imprint","INTERSECT",VERTEX,{"derivedFrom":[subQ1,subQ0]});Q64=makeQuery(id+"F0.imprint","IMPRINT",FACE,{"disambiguationData":[TD([[makeQuery(id+"F0.imprint","IMPRINT",EDGE,{"disambiguationData":[TD([[subQ2,1.0]])],"derivedFrom":subQ1}),-1.0]])]});}
            var Q65;
            {var subQ0=sQuery(id+"F0.wireOp",EDGE,"E6");var subQ1=sQuery(id+"F0.wireOp",EDGE,"E2.15.0");var subQ2=makeQuery(id+"F0.imprint","INTERSECT",VERTEX,{"derivedFrom":[subQ1,subQ0]});Q65=makeQuery(id+"F0.imprint","IMPRINT",FACE,{"disambiguationData":[TD([[makeQuery(id+"F0.imprint","IMPRINT",EDGE,{"disambiguationData":[TD([[subQ2,1.0]])],"derivedFrom":subQ1}),-1.0]])]});}
            var Q66;
            {var subQ0=sQuery(id+"F0.wireOp",EDGE,"E2.1.0");var subQ1=sQuery(id+"F0.wireOp",EDGE,"E0");var subQ2=makeQuery(id+"F0.imprint","INTERSECT",VERTEX,{"derivedFrom":[subQ1,subQ0]});Q66=makeQuery(id+"F0.imprint","IMPRINT",FACE,{"disambiguationData":[TD([[makeQuery(id+"F0.imprint","IMPRINT",EDGE,{"disambiguationData":[TD([[subQ2,-1.0]])],"derivedFrom":subQ1}),-1.0]])]});}
            var Q67;
            {var subQ0=sQuery(id+"F0.wireOp",EDGE,"E2.8.0");var subQ1=sQuery(id+"F0.wireOp",EDGE,"E0");var subQ2=makeQuery(id+"F0.imprint","INTERSECT",VERTEX,{"derivedFrom":[subQ1,subQ0]});Q67=makeQuery(id+"F0.imprint","IMPRINT",FACE,{"disambiguationData":[TD([[makeQuery(id+"F0.imprint","IMPRINT",EDGE,{"disambiguationData":[TD([[subQ2,-1.0]])],"derivedFrom":subQ1}),-1.0]])]});}
            var Q68;
            {var subQ0=sQuery(id+"F0.wireOp",EDGE,"E6");var subQ1=sQuery(id+"F0.wireOp",EDGE,"E2.8.0");var subQ2=makeQuery(id+"F0.imprint","INTERSECT",VERTEX,{"derivedFrom":[subQ1,subQ0]});Q68=makeQuery(id+"F0.imprint","IMPRINT",FACE,{"disambiguationData":[TD([[makeQuery(id+"F0.imprint","IMPRINT",EDGE,{"disambiguationData":[TD([[subQ2,1.0]])],"derivedFrom":subQ1}),1.0]])]});}
            var Q69;
            {var subQ0=sQuery(id+"F0.wireOp",EDGE,"E2.21.2");var subQ1=sQuery(id+"F0.wireOp",EDGE,"E0");var subQ2=makeQuery(id+"F0.imprint","INTERSECT",VERTEX,{"derivedFrom":[subQ1,subQ0]});Q69=makeQuery(id+"F0.imprint","IMPRINT",FACE,{"disambiguationData":[TD([[makeQuery(id+"F0.imprint","IMPRINT",EDGE,{"disambiguationData":[TD([[subQ2,-1.0]])],"derivedFrom":subQ1}),-1.0]])]});}
            var Q70;
            {var subQ0=sQuery(id+"F0.wireOp",EDGE,"E6");var subQ1=sQuery(id+"F0.wireOp",EDGE,"E2.8.0");var subQ2=makeQuery(id+"F0.imprint","INTERSECT",VERTEX,{"derivedFrom":[subQ1,subQ0]});Q70=makeQuery(id+"F0.imprint","IMPRINT",FACE,{"disambiguationData":[TD([[makeQuery(id+"F0.imprint","IMPRINT",EDGE,{"disambiguationData":[TD([[subQ2,1.0]])],"derivedFrom":subQ1}),-1.0]])]});}
            var Q71;
            {var subQ0=sQuery(id+"F0.wireOp",EDGE,"E2.10.1");Q71=makeQuery(id+"F0.imprint","IMPRINT",FACE,{"disambiguationData":[TD([[makeQuery(id+"F0.imprint","IMPRINT",EDGE,{"derivedFrom":subQ0}),1.0]])]});}
            var Q72;
            {var subQ0=sQuery(id+"F0.wireOp",EDGE,"E6");var subQ1=sQuery(id+"F0.wireOp",EDGE,"E2.7.0");var subQ2=makeQuery(id+"F0.imprint","INTERSECT",VERTEX,{"derivedFrom":[subQ1,subQ0]});Q72=makeQuery(id+"F0.imprint","IMPRINT",FACE,{"disambiguationData":[TD([[makeQuery(id+"F0.imprint","IMPRINT",EDGE,{"disambiguationData":[TD([[subQ2,1.0]])],"derivedFrom":subQ1}),-1.0]])]});}
            var Q73;
            {var subQ0=sQuery(id+"F0.wireOp",EDGE,"E6");var subQ1=sQuery(id+"F0.wireOp",EDGE,"E2.15.0");var subQ2=makeQuery(id+"F0.imprint","INTERSECT",VERTEX,{"derivedFrom":[subQ1,subQ0]});Q73=makeQuery(id+"F0.imprint","IMPRINT",FACE,{"disambiguationData":[TD([[makeQuery(id+"F0.imprint","IMPRINT",EDGE,{"disambiguationData":[TD([[subQ2,1.0]])],"derivedFrom":subQ1}),1.0]])]});}
            var Q74;
            {var subQ0=sQuery(id+"F0.wireOp",EDGE,"E2.19.0");var subQ1=sQuery(id+"F0.wireOp",EDGE,"E0");var subQ2=makeQuery(id+"F0.imprint","INTERSECT",VERTEX,{"derivedFrom":[subQ1,subQ0]});Q74=makeQuery(id+"F0.imprint","IMPRINT",FACE,{"disambiguationData":[TD([[makeQuery(id+"F0.imprint","IMPRINT",EDGE,{"disambiguationData":[TD([[subQ2,-1.0]])],"derivedFrom":subQ1}),-1.0]])]});}
            var Q75;
            {var subQ5=sQuery(id+"F0.wireOp",EDGE,"E2.19.3");Q75=makeQuery(id+"F0.imprint","IMPRINT",FACE,{"disambiguationData":[TD([[makeQuery(id+"F0.imprint","IMPRINT",EDGE,{"derivedFrom":subQ5}),-1.0]])]});}
            var Q76;
            {var subQ0=sQuery(id+"F0.wireOp",EDGE,"E2.17.2");var subQ1=sQuery(id+"F0.wireOp",EDGE,"E0");var subQ2=makeQuery(id+"F0.imprint","INTERSECT",VERTEX,{"derivedFrom":[subQ1,subQ0]});Q76=makeQuery(id+"F0.imprint","IMPRINT",FACE,{"disambiguationData":[TD([[makeQuery(id+"F0.imprint","IMPRINT",EDGE,{"disambiguationData":[TD([[subQ2,-1.0]])],"derivedFrom":subQ1}),-1.0]])]});}
            var Q77;
            {var subQ0=sQuery(id+"F0.wireOp",EDGE,"E6");var subQ1=sQuery(id+"F0.wireOp",EDGE,"E2.12.0");var subQ2=makeQuery(id+"F0.imprint","INTERSECT",VERTEX,{"derivedFrom":[subQ1,subQ0]});Q77=makeQuery(id+"F0.imprint","IMPRINT",FACE,{"disambiguationData":[TD([[makeQuery(id+"F0.imprint","IMPRINT",EDGE,{"disambiguationData":[TD([[subQ2,1.0]])],"derivedFrom":subQ1}),-1.0]])]});}
            var Q78;
            {var subQ0=sQuery(id+"F0.wireOp",EDGE,"E2.1.2");var subQ1=sQuery(id+"F0.wireOp",EDGE,"E0");var subQ2=makeQuery(id+"F0.imprint","INTERSECT",VERTEX,{"derivedFrom":[subQ1,subQ0]});Q78=makeQuery(id+"F0.imprint","IMPRINT",FACE,{"disambiguationData":[TD([[makeQuery(id+"F0.imprint","IMPRINT",EDGE,{"disambiguationData":[TD([[subQ2,-1.0]])],"derivedFrom":subQ1}),-1.0]])]});}
            var Q79;
            {var subQ0=sQuery(id+"F0.wireOp",EDGE,"E6");var subQ1=sQuery(id+"F0.wireOp",EDGE,"E2.6.0");var subQ2=makeQuery(id+"F0.imprint","INTERSECT",VERTEX,{"derivedFrom":[subQ1,subQ0]});Q79=makeQuery(id+"F0.imprint","IMPRINT",FACE,{"disambiguationData":[TD([[makeQuery(id+"F0.imprint","IMPRINT",EDGE,{"disambiguationData":[TD([[subQ2,1.0]])],"derivedFrom":subQ1}),-1.0]])]});}
            var Q80;
            {var subQ0=sQuery(id+"F0.wireOp",EDGE,"E2.23.2");var subQ1=sQuery(id+"F0.wireOp",EDGE,"E0");var subQ2=makeQuery(id+"F0.imprint","INTERSECT",VERTEX,{"derivedFrom":[subQ1,subQ0]});Q80=makeQuery(id+"F0.imprint","IMPRINT",FACE,{"disambiguationData":[TD([[makeQuery(id+"F0.imprint","IMPRINT",EDGE,{"disambiguationData":[TD([[subQ2,-1.0]])],"derivedFrom":subQ1}),-1.0]])]});}
            var Q81;
            {var subQ0=sQuery(id+"F0.wireOp",EDGE,"E6");var subQ1=sQuery(id+"F0.wireOp",EDGE,"E2.18.0");var subQ2=makeQuery(id+"F0.imprint","INTERSECT",VERTEX,{"derivedFrom":[subQ1,subQ0]});Q81=makeQuery(id+"F0.imprint","IMPRINT",FACE,{"disambiguationData":[TD([[makeQuery(id+"F0.imprint","IMPRINT",EDGE,{"disambiguationData":[TD([[subQ2,1.0]])],"derivedFrom":subQ1}),1.0]])]});}
            var Q82;
            {var subQ0=sQuery(id+"F0.wireOp",EDGE,"E1.right");var subQ1=sQuery(id+"F0.wireOp",EDGE,"E0");var subQ2=makeQuery(id+"F0.imprint","INTERSECT",VERTEX,{"derivedFrom":[subQ1,subQ0]});Q82=makeQuery(id+"F0.imprint","IMPRINT",FACE,{"disambiguationData":[TD([[makeQuery(id+"F0.imprint","IMPRINT",EDGE,{"disambiguationData":[TD([[subQ2,1.0]])],"derivedFrom":subQ1}),-1.0]])]});}
            var Q83;
            {var subQ0=sQuery(id+"F0.wireOp",EDGE,"E2.22.2");var subQ1=sQuery(id+"F0.wireOp",EDGE,"E0");var subQ2=makeQuery(id+"F0.imprint","INTERSECT",VERTEX,{"derivedFrom":[subQ1,subQ0]});Q83=makeQuery(id+"F0.imprint","IMPRINT",FACE,{"disambiguationData":[TD([[makeQuery(id+"F0.imprint","IMPRINT",EDGE,{"disambiguationData":[TD([[subQ2,-1.0]])],"derivedFrom":subQ1}),-1.0]])]});}
            var Q84;
            {var subQ0=sQuery(id+"F0.wireOp",EDGE,"E2.2.0");var subQ1=sQuery(id+"F0.wireOp",EDGE,"E0");var subQ2=makeQuery(id+"F0.imprint","INTERSECT",VERTEX,{"derivedFrom":[subQ1,subQ0]});Q84=makeQuery(id+"F0.imprint","IMPRINT",FACE,{"disambiguationData":[TD([[makeQuery(id+"F0.imprint","IMPRINT",EDGE,{"disambiguationData":[TD([[subQ2,-1.0]])],"derivedFrom":subQ1}),-1.0]])]});}
            var Q85;
            {var subQ0=sQuery(id+"F0.wireOp",EDGE,"E6");var subQ1=sQuery(id+"F0.wireOp",EDGE,"E2.23.0");var subQ2=makeQuery(id+"F0.imprint","INTERSECT",VERTEX,{"derivedFrom":[subQ1,subQ0]});Q85=makeQuery(id+"F0.imprint","IMPRINT",FACE,{"disambiguationData":[TD([[makeQuery(id+"F0.imprint","IMPRINT",EDGE,{"disambiguationData":[TD([[subQ2,1.0]])],"derivedFrom":subQ1}),-1.0]])]});}
            var Q86;
            {var subQ0=sQuery(id+"F0.wireOp",EDGE,"E2.15.2");var subQ1=sQuery(id+"F0.wireOp",EDGE,"E0");var subQ2=makeQuery(id+"F0.imprint","INTERSECT",VERTEX,{"derivedFrom":[subQ1,subQ0]});Q86=makeQuery(id+"F0.imprint","IMPRINT",FACE,{"disambiguationData":[TD([[makeQuery(id+"F0.imprint","IMPRINT",EDGE,{"disambiguationData":[TD([[subQ2,-1.0]])],"derivedFrom":subQ1}),-1.0]])]});}
            var Q87;
            {var subQ0=sQuery(id+"F0.wireOp",EDGE,"E2.18.1");Q87=makeQuery(id+"F0.imprint","IMPRINT",FACE,{"disambiguationData":[TD([[makeQuery(id+"F0.imprint","IMPRINT",EDGE,{"derivedFrom":subQ0}),1.0]])]});}
            var Q88;
            {var subQ0=sQuery(id+"F0.wireOp",EDGE,"E2.2.1");Q88=makeQuery(id+"F0.imprint","IMPRINT",FACE,{"disambiguationData":[TD([[makeQuery(id+"F0.imprint","IMPRINT",EDGE,{"derivedFrom":subQ0}),1.0]])]});}
            var Q89;
            {var subQ0=sQuery(id+"F0.wireOp",EDGE,"E6");var subQ1=sQuery(id+"F0.wireOp",EDGE,"E1.left");var subQ2=makeQuery(id+"F0.imprint","INTERSECT",VERTEX,{"derivedFrom":[subQ1,subQ0]});Q89=makeQuery(id+"F0.imprint","IMPRINT",FACE,{"disambiguationData":[TD([[makeQuery(id+"F0.imprint","IMPRINT",EDGE,{"disambiguationData":[TD([[subQ2,1.0]])],"derivedFrom":subQ1}),1.0]])]});}
            var Q90;
            {var subQ0=sQuery(id+"F0.wireOp",EDGE,"E2.11.2");var subQ1=sQuery(id+"F0.wireOp",EDGE,"E0");var subQ2=makeQuery(id+"F0.imprint","INTERSECT",VERTEX,{"derivedFrom":[subQ1,subQ0]});Q90=makeQuery(id+"F0.imprint","IMPRINT",FACE,{"disambiguationData":[TD([[makeQuery(id+"F0.imprint","IMPRINT",EDGE,{"disambiguationData":[TD([[subQ2,-1.0]])],"derivedFrom":subQ1}),-1.0]])]});}
            var Q91;
            {var subQ0=sQuery(id+"F0.wireOp",EDGE,"E2.12.1");Q91=makeQuery(id+"F0.imprint","IMPRINT",FACE,{"disambiguationData":[TD([[makeQuery(id+"F0.imprint","IMPRINT",EDGE,{"derivedFrom":subQ0}),1.0]])]});}
            var Q92;
            {var subQ0=sQuery(id+"F0.wireOp",EDGE,"E2.14.0");var subQ1=sQuery(id+"F0.wireOp",EDGE,"E0");var subQ2=makeQuery(id+"F0.imprint","INTERSECT",VERTEX,{"derivedFrom":[subQ1,subQ0]});Q92=makeQuery(id+"F0.imprint","IMPRINT",FACE,{"disambiguationData":[TD([[makeQuery(id+"F0.imprint","IMPRINT",EDGE,{"disambiguationData":[TD([[subQ2,-1.0]])],"derivedFrom":subQ1}),-1.0]])]});}
            var Q93;
            {var subQ0=sQuery(id+"F0.wireOp",EDGE,"E6");var subQ1=sQuery(id+"F0.wireOp",EDGE,"E2.18.0");var subQ2=makeQuery(id+"F0.imprint","INTERSECT",VERTEX,{"derivedFrom":[subQ1,subQ0]});Q93=makeQuery(id+"F0.imprint","IMPRINT",FACE,{"disambiguationData":[TD([[makeQuery(id+"F0.imprint","IMPRINT",EDGE,{"disambiguationData":[TD([[subQ2,1.0]])],"derivedFrom":subQ1}),-1.0]])]});}
            var Q94;
            {var subQ0=sQuery(id+"F0.wireOp",EDGE,"E6");var subQ1=sQuery(id+"F0.wireOp",EDGE,"E2.16.0");var subQ2=makeQuery(id+"F0.imprint","INTERSECT",VERTEX,{"derivedFrom":[subQ1,subQ0]});Q94=makeQuery(id+"F0.imprint","IMPRINT",FACE,{"disambiguationData":[TD([[makeQuery(id+"F0.imprint","IMPRINT",EDGE,{"disambiguationData":[TD([[subQ2,1.0]])],"derivedFrom":subQ1}),1.0]])]});}
            var Q95;
            {var subQ0=sQuery(id+"F0.wireOp",EDGE,"E2.22.1");Q95=makeQuery(id+"F0.imprint","IMPRINT",FACE,{"disambiguationData":[TD([[makeQuery(id+"F0.imprint","IMPRINT",EDGE,{"derivedFrom":subQ0}),1.0]])]});}
            var Q96;
            {var subQ0=sQuery(id+"F0.wireOp",EDGE,"E2.13.0");var subQ1=sQuery(id+"F0.wireOp",EDGE,"E0");var subQ2=makeQuery(id+"F0.imprint","INTERSECT",VERTEX,{"derivedFrom":[subQ1,subQ0]});Q96=makeQuery(id+"F0.imprint","IMPRINT",FACE,{"disambiguationData":[TD([[makeQuery(id+"F0.imprint","IMPRINT",EDGE,{"disambiguationData":[TD([[subQ2,-1.0]])],"derivedFrom":subQ1}),-1.0]])]});}
            var Q97;
            {var subQ0=sQuery(id+"F0.wireOp",EDGE,"E6");var subQ1=sQuery(id+"F0.wireOp",EDGE,"E2.17.0");var subQ2=makeQuery(id+"F0.imprint","INTERSECT",VERTEX,{"derivedFrom":[subQ1,subQ0]});Q97=makeQuery(id+"F0.imprint","IMPRINT",FACE,{"disambiguationData":[TD([[makeQuery(id+"F0.imprint","IMPRINT",EDGE,{"disambiguationData":[TD([[subQ2,1.0]])],"derivedFrom":subQ1}),1.0]])]});}
            var Q98;
            {var subQ0=sQuery(id+"F0.wireOp",EDGE,"E2.4.1");Q98=makeQuery(id+"F0.imprint","IMPRINT",FACE,{"disambiguationData":[TD([[makeQuery(id+"F0.imprint","IMPRINT",EDGE,{"derivedFrom":subQ0}),1.0]])]});}
            var Q99;
            {var subQ0=sQuery(id+"F0.wireOp",EDGE,"E2.12.2");var subQ1=sQuery(id+"F0.wireOp",EDGE,"E0");var subQ2=makeQuery(id+"F0.imprint","INTERSECT",VERTEX,{"derivedFrom":[subQ1,subQ0]});Q99=makeQuery(id+"F0.imprint","IMPRINT",FACE,{"disambiguationData":[TD([[makeQuery(id+"F0.imprint","IMPRINT",EDGE,{"disambiguationData":[TD([[subQ2,-1.0]])],"derivedFrom":subQ1}),-1.0]])]});}
            var Q100;
            {var subQ0=sQuery(id+"F0.wireOp",EDGE,"E6");var subQ1=sQuery(id+"F0.wireOp",EDGE,"E2.11.0");var subQ2=makeQuery(id+"F0.imprint","INTERSECT",VERTEX,{"derivedFrom":[subQ1,subQ0]});Q100=makeQuery(id+"F0.imprint","IMPRINT",FACE,{"disambiguationData":[TD([[makeQuery(id+"F0.imprint","IMPRINT",EDGE,{"disambiguationData":[TD([[subQ2,1.0]])],"derivedFrom":subQ1}),1.0]])]});}
            var Q101;
            {var subQ0=sQuery(id+"F0.wireOp",EDGE,"E2.21.0");var subQ1=sQuery(id+"F0.wireOp",EDGE,"E0");var subQ2=makeQuery(id+"F0.imprint","INTERSECT",VERTEX,{"derivedFrom":[subQ1,subQ0]});Q101=makeQuery(id+"F0.imprint","IMPRINT",FACE,{"disambiguationData":[TD([[makeQuery(id+"F0.imprint","IMPRINT",EDGE,{"disambiguationData":[TD([[subQ2,-1.0]])],"derivedFrom":subQ1}),-1.0]])]});}
            var Q102;
            {var subQ0=sQuery(id+"F0.wireOp",EDGE,"E6");var subQ1=sQuery(id+"F0.wireOp",EDGE,"E2.9.0");var subQ2=makeQuery(id+"F0.imprint","INTERSECT",VERTEX,{"derivedFrom":[subQ1,subQ0]});Q102=makeQuery(id+"F0.imprint","IMPRINT",FACE,{"disambiguationData":[TD([[makeQuery(id+"F0.imprint","IMPRINT",EDGE,{"disambiguationData":[TD([[subQ2,1.0]])],"derivedFrom":subQ1}),1.0]])]});}
            var Q103;
            {var subQ0=sQuery(id+"F0.wireOp",EDGE,"E2.14.1");Q103=makeQuery(id+"F0.imprint","IMPRINT",FACE,{"disambiguationData":[TD([[makeQuery(id+"F0.imprint","IMPRINT",EDGE,{"derivedFrom":subQ0}),1.0]])]});}
            var Q104;
            {var subQ0=sQuery(id+"F0.wireOp",EDGE,"E6");var subQ1=sQuery(id+"F0.wireOp",EDGE,"E2.5.0");var subQ2=makeQuery(id+"F0.imprint","INTERSECT",VERTEX,{"derivedFrom":[subQ1,subQ0]});Q104=makeQuery(id+"F0.imprint","IMPRINT",FACE,{"disambiguationData":[TD([[makeQuery(id+"F0.imprint","IMPRINT",EDGE,{"disambiguationData":[TD([[subQ2,1.0]])],"derivedFrom":subQ1}),-1.0]])]});}
            var Q105;
            {var subQ0=sQuery(id+"F0.wireOp",EDGE,"E2.8.2");var subQ1=sQuery(id+"F0.wireOp",EDGE,"E0");var subQ2=makeQuery(id+"F0.imprint","INTERSECT",VERTEX,{"derivedFrom":[subQ1,subQ0]});Q105=makeQuery(id+"F0.imprint","IMPRINT",FACE,{"disambiguationData":[TD([[makeQuery(id+"F0.imprint","IMPRINT",EDGE,{"disambiguationData":[TD([[subQ2,-1.0]])],"derivedFrom":subQ1}),-1.0]])]});}
            var Q106;
            {var subQ0=sQuery(id+"F0.wireOp",EDGE,"E3.6.24.0");var subQ1=sQuery(id+"F0.wireOp",EDGE,"E0");var subQ2=makeQuery(id+"F0.imprint","INTERSECT",VERTEX,{"derivedFrom":[subQ1,subQ0]});Q106=makeQuery(id+"F0.imprint","IMPRINT",FACE,{"disambiguationData":[TD([[makeQuery(id+"F0.imprint","IMPRINT",EDGE,{"disambiguationData":[TD([[subQ2,-1.0]])],"derivedFrom":subQ1}),-1.0]])]});}
            var Q107;
            {var subQ0=sQuery(id+"F0.wireOp",EDGE,"E2.8.1");Q107=makeQuery(id+"F0.imprint","IMPRINT",FACE,{"disambiguationData":[TD([[makeQuery(id+"F0.imprint","IMPRINT",EDGE,{"derivedFrom":subQ0}),1.0]])]});}
            var Q108;
            {var subQ0=sQuery(id+"F0.wireOp",EDGE,"E6");var subQ1=sQuery(id+"F0.wireOp",EDGE,"E2.7.0");var subQ2=makeQuery(id+"F0.imprint","INTERSECT",VERTEX,{"derivedFrom":[subQ1,subQ0]});Q108=makeQuery(id+"F0.imprint","IMPRINT",FACE,{"disambiguationData":[TD([[makeQuery(id+"F0.imprint","IMPRINT",EDGE,{"disambiguationData":[TD([[subQ2,1.0]])],"derivedFrom":subQ1}),1.0]])]});}
            var Q109;
            {var subQ0=sQuery(id+"F0.wireOp",EDGE,"E2.15.1");Q109=makeQuery(id+"F0.imprint","IMPRINT",FACE,{"disambiguationData":[TD([[makeQuery(id+"F0.imprint","IMPRINT",EDGE,{"derivedFrom":subQ0}),1.0]])]});}
            var Q110;
            {var subQ0=sQuery(id+"F0.wireOp",EDGE,"E2.20.0");var subQ1=sQuery(id+"F0.wireOp",EDGE,"E0");var subQ2=makeQuery(id+"F0.imprint","INTERSECT",VERTEX,{"derivedFrom":[subQ1,subQ0]});Q110=makeQuery(id+"F0.imprint","IMPRINT",FACE,{"disambiguationData":[TD([[makeQuery(id+"F0.imprint","IMPRINT",EDGE,{"disambiguationData":[TD([[subQ2,-1.0]])],"derivedFrom":subQ1}),-1.0]])]});}
            var Q111;
            {var subQ0=sQuery(id+"F0.wireOp",EDGE,"E2.7.2");var subQ1=sQuery(id+"F0.wireOp",EDGE,"E0");var subQ2=makeQuery(id+"F0.imprint","INTERSECT",VERTEX,{"derivedFrom":[subQ1,subQ0]});Q111=makeQuery(id+"F0.imprint","IMPRINT",FACE,{"disambiguationData":[TD([[makeQuery(id+"F0.imprint","IMPRINT",EDGE,{"disambiguationData":[TD([[subQ2,-1.0]])],"derivedFrom":subQ1}),-1.0]])]});}
            var Q112;
            {var subQ0=sQuery(id+"F0.wireOp",EDGE,"E6");var subQ1=sQuery(id+"F0.wireOp",EDGE,"E2.2.0");var subQ2=makeQuery(id+"F0.imprint","INTERSECT",VERTEX,{"derivedFrom":[subQ1,subQ0]});Q112=makeQuery(id+"F0.imprint","IMPRINT",FACE,{"disambiguationData":[TD([[makeQuery(id+"F0.imprint","IMPRINT",EDGE,{"disambiguationData":[TD([[subQ2,1.0]])],"derivedFrom":subQ1}),1.0]])]});}
            var Q113;
            {var subQ0=sQuery(id+"F0.wireOp",EDGE,"E2.12.0");var subQ1=sQuery(id+"F0.wireOp",EDGE,"E0");var subQ2=makeQuery(id+"F0.imprint","INTERSECT",VERTEX,{"derivedFrom":[subQ1,subQ0]});Q113=makeQuery(id+"F0.imprint","IMPRINT",FACE,{"disambiguationData":[TD([[makeQuery(id+"F0.imprint","IMPRINT",EDGE,{"disambiguationData":[TD([[subQ2,-1.0]])],"derivedFrom":subQ1}),-1.0]])]});}
            var Q114;
            {var subQ0=sQuery(id+"F0.wireOp",EDGE,"E2.23.1");Q114=makeQuery(id+"F0.imprint","IMPRINT",FACE,{"disambiguationData":[TD([[makeQuery(id+"F0.imprint","IMPRINT",EDGE,{"derivedFrom":subQ0}),1.0]])]});}
            var Q115;
            {var subQ0=sQuery(id+"F0.wireOp",EDGE,"E4");var subQ1=sQuery(id+"F0.wireOp",EDGE,"E1.left");var subQ2=makeQuery(id+"F0.imprint","INTERSECT",VERTEX,{"derivedFrom":[subQ1,subQ0]});Q115=makeQuery(id+"F0.imprint","IMPRINT",FACE,{"disambiguationData":[TD([[makeQuery(id+"F0.imprint","IMPRINT",EDGE,{"disambiguationData":[TD([[subQ2,-1.0]])],"derivedFrom":subQ1}),1.0]])]});}
            var Q116;
            {var subQ0=sQuery(id+"F0.wireOp",EDGE,"E2.9.2");var subQ1=sQuery(id+"F0.wireOp",EDGE,"E0");var subQ2=makeQuery(id+"F0.imprint","INTERSECT",VERTEX,{"derivedFrom":[subQ1,subQ0]});Q116=makeQuery(id+"F0.imprint","IMPRINT",FACE,{"disambiguationData":[TD([[makeQuery(id+"F0.imprint","IMPRINT",EDGE,{"disambiguationData":[TD([[subQ2,-1.0]])],"derivedFrom":subQ1}),-1.0]])]});}
            var Q117;
            {var subQ0=sQuery(id+"F0.wireOp",EDGE,"E6");var subQ1=sQuery(id+"F0.wireOp",EDGE,"E2.10.0");var subQ2=makeQuery(id+"F0.imprint","INTERSECT",VERTEX,{"derivedFrom":[subQ1,subQ0]});Q117=makeQuery(id+"F0.imprint","IMPRINT",FACE,{"disambiguationData":[TD([[makeQuery(id+"F0.imprint","IMPRINT",EDGE,{"disambiguationData":[TD([[subQ2,1.0]])],"derivedFrom":subQ1}),1.0]])]});}
            var Q118;
            {var subQ0=sQuery(id+"F0.wireOp",EDGE,"E6");var subQ1=sQuery(id+"F0.wireOp",EDGE,"E2.14.0");var subQ2=makeQuery(id+"F0.imprint","INTERSECT",VERTEX,{"derivedFrom":[subQ1,subQ0]});Q118=makeQuery(id+"F0.imprint","IMPRINT",FACE,{"disambiguationData":[TD([[makeQuery(id+"F0.imprint","IMPRINT",EDGE,{"disambiguationData":[TD([[subQ2,1.0]])],"derivedFrom":subQ1}),-1.0]])]});}
            var Q119;
            {var subQ0=sQuery(id+"F0.wireOp",EDGE,"E6");var subQ1=sQuery(id+"F0.wireOp",EDGE,"E2.1.0");var subQ2=makeQuery(id+"F0.imprint","INTERSECT",VERTEX,{"derivedFrom":[subQ1,subQ0]});Q119=makeQuery(id+"F0.imprint","IMPRINT",FACE,{"disambiguationData":[TD([[makeQuery(id+"F0.imprint","IMPRINT",EDGE,{"disambiguationData":[TD([[subQ2,1.0]])],"derivedFrom":subQ1}),-1.0]])]});}
            var Q120;
            {var subQ0=sQuery(id+"F0.wireOp",EDGE,"E6");var subQ1=sQuery(id+"F0.wireOp",EDGE,"E2.17.0");var subQ2=makeQuery(id+"F0.imprint","INTERSECT",VERTEX,{"derivedFrom":[subQ1,subQ0]});Q120=makeQuery(id+"F0.imprint","IMPRINT",FACE,{"disambiguationData":[TD([[makeQuery(id+"F0.imprint","IMPRINT",EDGE,{"disambiguationData":[TD([[subQ2,1.0]])],"derivedFrom":subQ1}),-1.0]])]});}
            var Q121;
            {var subQ0=sQuery(id+"F0.wireOp",EDGE,"E2.20.1");Q121=makeQuery(id+"F0.imprint","IMPRINT",FACE,{"disambiguationData":[TD([[makeQuery(id+"F0.imprint","IMPRINT",EDGE,{"derivedFrom":subQ0}),1.0]])]});}
            var Q122;
            {var subQ0=sQuery(id+"F0.wireOp",EDGE,"E2.13.1");Q122=makeQuery(id+"F0.imprint","IMPRINT",FACE,{"disambiguationData":[TD([[makeQuery(id+"F0.imprint","IMPRINT",EDGE,{"derivedFrom":subQ0}),1.0]])]});}
            var Q123;
            {var subQ0=sQuery(id+"F0.wireOp",EDGE,"E6");var subQ1=sQuery(id+"F0.wireOp",EDGE,"E2.3.0");var subQ2=makeQuery(id+"F0.imprint","INTERSECT",VERTEX,{"derivedFrom":[subQ1,subQ0]});Q123=makeQuery(id+"F0.imprint","IMPRINT",FACE,{"disambiguationData":[TD([[makeQuery(id+"F0.imprint","IMPRINT",EDGE,{"disambiguationData":[TD([[subQ2,1.0]])],"derivedFrom":subQ1}),-1.0]])]});}
            var Q124;
            {var subQ0=sQuery(id+"F0.wireOp",EDGE,"E6");var subQ1=sQuery(id+"F0.wireOp",EDGE,"E2.10.0");var subQ2=makeQuery(id+"F0.imprint","INTERSECT",VERTEX,{"derivedFrom":[subQ1,subQ0]});Q124=makeQuery(id+"F0.imprint","IMPRINT",FACE,{"disambiguationData":[TD([[makeQuery(id+"F0.imprint","IMPRINT",EDGE,{"disambiguationData":[TD([[subQ2,1.0]])],"derivedFrom":subQ1}),-1.0]])]});}
            var Q125;
            {var subQ0=sQuery(id+"F0.wireOp",EDGE,"E6");var subQ1=sQuery(id+"F0.wireOp",EDGE,"E2.16.0");var subQ2=makeQuery(id+"F0.imprint","INTERSECT",VERTEX,{"derivedFrom":[subQ1,subQ0]});Q125=makeQuery(id+"F0.imprint","IMPRINT",FACE,{"disambiguationData":[TD([[makeQuery(id+"F0.imprint","IMPRINT",EDGE,{"disambiguationData":[TD([[subQ2,1.0]])],"derivedFrom":subQ1}),-1.0]])]});}
            var Q126;
            {var subQ0=sQuery(id+"F0.wireOp",EDGE,"E2.16.0");var subQ1=sQuery(id+"F0.wireOp",EDGE,"E0");var subQ2=makeQuery(id+"F0.imprint","INTERSECT",VERTEX,{"derivedFrom":[subQ1,subQ0]});Q126=makeQuery(id+"F0.imprint","IMPRINT",FACE,{"disambiguationData":[TD([[makeQuery(id+"F0.imprint","IMPRINT",EDGE,{"disambiguationData":[TD([[subQ2,-1.0]])],"derivedFrom":subQ1}),-1.0]])]});}
            var Q127;
            {var subQ0=sQuery(id+"F0.wireOp",EDGE,"E2.19.1");Q127=makeQuery(id+"F0.imprint","IMPRINT",FACE,{"disambiguationData":[TD([[makeQuery(id+"F0.imprint","IMPRINT",EDGE,{"derivedFrom":subQ0}),1.0]])]});}
            var Q128;
            {var subQ0=sQuery(id+"F0.wireOp",EDGE,"E2.23.0");var subQ1=sQuery(id+"F0.wireOp",EDGE,"E0");var subQ2=makeQuery(id+"F0.imprint","INTERSECT",VERTEX,{"derivedFrom":[subQ1,subQ0]});Q128=makeQuery(id+"F0.imprint","IMPRINT",FACE,{"disambiguationData":[TD([[makeQuery(id+"F0.imprint","IMPRINT",EDGE,{"disambiguationData":[TD([[subQ2,-1.0]])],"derivedFrom":subQ1}),-1.0]])]});}
            var Q129;
            {var subQ0=sQuery(id+"F0.wireOp",EDGE,"E6");var subQ1=sQuery(id+"F0.wireOp",EDGE,"E2.3.0");var subQ2=makeQuery(id+"F0.imprint","INTERSECT",VERTEX,{"derivedFrom":[subQ1,subQ0]});Q129=makeQuery(id+"F0.imprint","IMPRINT",FACE,{"disambiguationData":[TD([[makeQuery(id+"F0.imprint","IMPRINT",EDGE,{"disambiguationData":[TD([[subQ2,1.0]])],"derivedFrom":subQ1}),1.0]])]});}
            var Q130;
            {var subQ0=sQuery(id+"F0.wireOp",EDGE,"E6");var subQ1=sQuery(id+"F0.wireOp",EDGE,"E2.6.0");var subQ2=makeQuery(id+"F0.imprint","INTERSECT",VERTEX,{"derivedFrom":[subQ1,subQ0]});Q130=makeQuery(id+"F0.imprint","IMPRINT",FACE,{"disambiguationData":[TD([[makeQuery(id+"F0.imprint","IMPRINT",EDGE,{"disambiguationData":[TD([[subQ2,1.0]])],"derivedFrom":subQ1}),1.0]])]});}
            var Q131;
            {var subQ0=sQuery(id+"F0.wireOp",EDGE,"E2.5.1");Q131=makeQuery(id+"F0.imprint","IMPRINT",FACE,{"disambiguationData":[TD([[makeQuery(id+"F0.imprint","IMPRINT",EDGE,{"derivedFrom":subQ0}),1.0]])]});}
            var Q132;
            {var subQ0=sQuery(id+"F0.wireOp",EDGE,"E2.21.1");Q132=makeQuery(id+"F0.imprint","IMPRINT",FACE,{"disambiguationData":[TD([[makeQuery(id+"F0.imprint","IMPRINT",EDGE,{"derivedFrom":subQ0}),1.0]])]});}
            var Q133;
            {var subQ0=sQuery(id+"F0.wireOp",EDGE,"E2.17.0");var subQ1=sQuery(id+"F0.wireOp",EDGE,"E0");var subQ2=makeQuery(id+"F0.imprint","INTERSECT",VERTEX,{"derivedFrom":[subQ1,subQ0]});Q133=makeQuery(id+"F0.imprint","IMPRINT",FACE,{"disambiguationData":[TD([[makeQuery(id+"F0.imprint","IMPRINT",EDGE,{"disambiguationData":[TD([[subQ2,-1.0]])],"derivedFrom":subQ1}),-1.0]])]});}
            var Q134;
            {var subQ0=sQuery(id+"F0.wireOp",EDGE,"E2.14.2");var subQ1=sQuery(id+"F0.wireOp",EDGE,"E0");var subQ2=makeQuery(id+"F0.imprint","INTERSECT",VERTEX,{"derivedFrom":[subQ1,subQ0]});Q134=makeQuery(id+"F0.imprint","IMPRINT",FACE,{"disambiguationData":[TD([[makeQuery(id+"F0.imprint","IMPRINT",EDGE,{"disambiguationData":[TD([[subQ2,-1.0]])],"derivedFrom":subQ1}),-1.0]])]});}
            var Q135;
            {var subQ0=sQuery(id+"F0.wireOp",EDGE,"E2.11.1");Q135=makeQuery(id+"F0.imprint","IMPRINT",FACE,{"disambiguationData":[TD([[makeQuery(id+"F0.imprint","IMPRINT",EDGE,{"derivedFrom":subQ0}),1.0]])]});}
            var Q136;
            {var subQ0=sQuery(id+"F0.wireOp",EDGE,"E2.5.2");var subQ1=sQuery(id+"F0.wireOp",EDGE,"E0");var subQ2=makeQuery(id+"F0.imprint","INTERSECT",VERTEX,{"derivedFrom":[subQ1,subQ0]});Q136=makeQuery(id+"F0.imprint","IMPRINT",FACE,{"disambiguationData":[TD([[makeQuery(id+"F0.imprint","IMPRINT",EDGE,{"disambiguationData":[TD([[subQ2,-1.0]])],"derivedFrom":subQ1}),-1.0]])]});}
            var Q137;
            {var subQ5=sQuery(id+"F0.wireOp",EDGE,"E2.1.3");Q137=makeQuery(id+"F0.imprint","IMPRINT",FACE,{"disambiguationData":[TD([[makeQuery(id+"F0.imprint","IMPRINT",EDGE,{"derivedFrom":subQ5}),-1.0]])]});}
            var Q138;
            {var subQ0=sQuery(id+"F0.wireOp",EDGE,"E2.9.1");Q138=makeQuery(id+"F0.imprint","IMPRINT",FACE,{"disambiguationData":[TD([[makeQuery(id+"F0.imprint","IMPRINT",EDGE,{"derivedFrom":subQ0}),1.0]])]});}
            var Q139;
            {var subQ5=sQuery(id+"F0.wireOp",EDGE,"E2.5.3");Q139=makeQuery(id+"F0.imprint","IMPRINT",FACE,{"disambiguationData":[TD([[makeQuery(id+"F0.imprint","IMPRINT",EDGE,{"derivedFrom":subQ5}),-1.0]])]});}
            var Q140;
            {var subQ0=sQuery(id+"F0.wireOp",EDGE,"E2.1.1");Q140=makeQuery(id+"F0.imprint","IMPRINT",FACE,{"disambiguationData":[TD([[makeQuery(id+"F0.imprint","IMPRINT",EDGE,{"derivedFrom":subQ0}),1.0]])]});}
            var Q141;
            {var subQ0=sQuery(id+"F0.wireOp",EDGE,"E2.3.1");Q141=makeQuery(id+"F0.imprint","IMPRINT",FACE,{"disambiguationData":[TD([[makeQuery(id+"F0.imprint","IMPRINT",EDGE,{"derivedFrom":subQ0}),1.0]])]});}
            var Q142;
            {var subQ5=sQuery(id+"F0.wireOp",EDGE,"E2.8.3");Q142=makeQuery(id+"F0.imprint","IMPRINT",FACE,{"disambiguationData":[TD([[makeQuery(id+"F0.imprint","IMPRINT",EDGE,{"derivedFrom":subQ5}),-1.0]])]});}
            var Q143;
            {var subQ5=sQuery(id+"F0.wireOp",EDGE,"E2.10.3");Q143=makeQuery(id+"F0.imprint","IMPRINT",FACE,{"disambiguationData":[TD([[makeQuery(id+"F0.imprint","IMPRINT",EDGE,{"derivedFrom":subQ5}),-1.0]])]});}
            var Q144;
            {var subQ5=sQuery(id+"F0.wireOp",EDGE,"E2.9.3");Q144=makeQuery(id+"F0.imprint","IMPRINT",FACE,{"disambiguationData":[TD([[makeQuery(id+"F0.imprint","IMPRINT",EDGE,{"derivedFrom":subQ5}),-1.0]])]});}
            var Q145;
            {var subQ5=sQuery(id+"F0.wireOp",EDGE,"E2.7.3");Q145=makeQuery(id+"F0.imprint","IMPRINT",FACE,{"disambiguationData":[TD([[makeQuery(id+"F0.imprint","IMPRINT",EDGE,{"derivedFrom":subQ5}),-1.0]])]});}
            var Q146;
            {var subQ5=sQuery(id+"F0.wireOp",EDGE,"E2.23.3");Q146=makeQuery(id+"F0.imprint","IMPRINT",FACE,{"disambiguationData":[TD([[makeQuery(id+"F0.imprint","IMPRINT",EDGE,{"derivedFrom":subQ5}),-1.0]])]});}
            var Q147;
            {var subQ5=sQuery(id+"F0.wireOp",EDGE,"E2.22.3");Q147=makeQuery(id+"F0.imprint","IMPRINT",FACE,{"disambiguationData":[TD([[makeQuery(id+"F0.imprint","IMPRINT",EDGE,{"derivedFrom":subQ5}),-1.0]])]});}
            var Q148;
            {var subQ5=sQuery(id+"F0.wireOp",EDGE,"E2.21.3");Q148=makeQuery(id+"F0.imprint","IMPRINT",FACE,{"disambiguationData":[TD([[makeQuery(id+"F0.imprint","IMPRINT",EDGE,{"derivedFrom":subQ5}),-1.0]])]});}
            var Q149;
            {var subQ5=sQuery(id+"F0.wireOp",EDGE,"E2.20.3");Q149=makeQuery(id+"F0.imprint","IMPRINT",FACE,{"disambiguationData":[TD([[makeQuery(id+"F0.imprint","IMPRINT",EDGE,{"derivedFrom":subQ5}),-1.0]])]});}
            var Q150;
            {var subQ5=sQuery(id+"F0.wireOp",EDGE,"E2.18.3");Q150=makeQuery(id+"F0.imprint","IMPRINT",FACE,{"disambiguationData":[TD([[makeQuery(id+"F0.imprint","IMPRINT",EDGE,{"derivedFrom":subQ5}),-1.0]])]});}
            var Q151;
            {var subQ5=sQuery(id+"F0.wireOp",EDGE,"E2.17.3");Q151=makeQuery(id+"F0.imprint","IMPRINT",FACE,{"disambiguationData":[TD([[makeQuery(id+"F0.imprint","IMPRINT",EDGE,{"derivedFrom":subQ5}),-1.0]])]});}
            var Q152;
            {var subQ5=sQuery(id+"F0.wireOp",EDGE,"E2.15.3");Q152=makeQuery(id+"F0.imprint","IMPRINT",FACE,{"disambiguationData":[TD([[makeQuery(id+"F0.imprint","IMPRINT",EDGE,{"derivedFrom":subQ5}),-1.0]])]});}
            var Q153;
            {var subQ5=sQuery(id+"F0.wireOp",EDGE,"E2.14.3");Q153=makeQuery(id+"F0.imprint","IMPRINT",FACE,{"disambiguationData":[TD([[makeQuery(id+"F0.imprint","IMPRINT",EDGE,{"derivedFrom":subQ5}),-1.0]])]});}
            var Q154;
            {var subQ5=sQuery(id+"F0.wireOp",EDGE,"E2.16.3");Q154=makeQuery(id+"F0.imprint","IMPRINT",FACE,{"disambiguationData":[TD([[makeQuery(id+"F0.imprint","IMPRINT",EDGE,{"derivedFrom":subQ5}),-1.0]])]});}
            var Q155;
            {var subQ5=sQuery(id+"F0.wireOp",EDGE,"E2.13.3");Q155=makeQuery(id+"F0.imprint","IMPRINT",FACE,{"disambiguationData":[TD([[makeQuery(id+"F0.imprint","IMPRINT",EDGE,{"derivedFrom":subQ5}),-1.0]])]});}
            var Q156;
            {var subQ5=sQuery(id+"F0.wireOp",EDGE,"E2.12.3");Q156=makeQuery(id+"F0.imprint","IMPRINT",FACE,{"disambiguationData":[TD([[makeQuery(id+"F0.imprint","IMPRINT",EDGE,{"derivedFrom":subQ5}),-1.0]])]});}
            var Q157;
            {var subQ5=sQuery(id+"F0.wireOp",EDGE,"E2.11.3");Q157=makeQuery(id+"F0.imprint","IMPRINT",FACE,{"disambiguationData":[TD([[makeQuery(id+"F0.imprint","IMPRINT",EDGE,{"derivedFrom":subQ5}),-1.0]])]});}
            var Q158;
            {var subQ5=sQuery(id+"F0.wireOp",EDGE,"E1.bottom");Q158=makeQuery(id+"F0.imprint","IMPRINT",FACE,{"disambiguationData":[TD([[makeQuery(id+"F0.imprint","IMPRINT",EDGE,{"derivedFrom":subQ5}),-1.0]])]});}
            var Q159;
            {var subQ5=sQuery(id+"F0.wireOp",EDGE,"E2.6.3");Q159=makeQuery(id+"F0.imprint","IMPRINT",FACE,{"disambiguationData":[TD([[makeQuery(id+"F0.imprint","IMPRINT",EDGE,{"derivedFrom":subQ5}),-1.0]])]});}
            var Q160;
            {var subQ0=sQuery(id+"F0.wireOp",EDGE,"E2.16.1");Q160=makeQuery(id+"F0.imprint","IMPRINT",FACE,{"disambiguationData":[TD([[makeQuery(id+"F0.imprint","IMPRINT",EDGE,{"derivedFrom":subQ0}),1.0]])]});}
            var Q161;
            {var subQ0=sQuery(id+"F0.wireOp",EDGE,"E1.top");Q161=makeQuery(id+"F0.imprint","IMPRINT",FACE,{"disambiguationData":[TD([[makeQuery(id+"F0.imprint","IMPRINT",EDGE,{"derivedFrom":subQ0}),1.0]])]});}
            var Q162;
            {var subQ0=sQuery(id+"F0.wireOp",EDGE,"E2.17.1");Q162=makeQuery(id+"F0.imprint","IMPRINT",FACE,{"disambiguationData":[TD([[makeQuery(id+"F0.imprint","IMPRINT",EDGE,{"derivedFrom":subQ0}),1.0]])]});}
            var Q163;
            {var subQ0=sQuery(id+"F0.wireOp",EDGE,"E2.7.1");Q163=makeQuery(id+"F0.imprint","IMPRINT",FACE,{"disambiguationData":[TD([[makeQuery(id+"F0.imprint","IMPRINT",EDGE,{"derivedFrom":subQ0}),1.0]])]});}
            var Q164;
            {var subQ0=sQuery(id+"F0.wireOp",EDGE,"E2.6.1");Q164=makeQuery(id+"F0.imprint","IMPRINT",FACE,{"disambiguationData":[TD([[makeQuery(id+"F0.imprint","IMPRINT",EDGE,{"derivedFrom":subQ0}),1.0]])]});}
            var Q165;
            {var subQ5=sQuery(id+"F0.wireOp",EDGE,"E2.2.3");Q165=makeQuery(id+"F0.imprint","IMPRINT",FACE,{"disambiguationData":[TD([[makeQuery(id+"F0.imprint","IMPRINT",EDGE,{"derivedFrom":subQ5}),-1.0]])]});}
            var Q166;
            {var subQ5=sQuery(id+"F0.wireOp",EDGE,"E2.3.3");Q166=makeQuery(id+"F0.imprint","IMPRINT",FACE,{"disambiguationData":[TD([[makeQuery(id+"F0.imprint","IMPRINT",EDGE,{"derivedFrom":subQ5}),-1.0]])]});}
            var Q167;
            {var subQ5=sQuery(id+"F0.wireOp",EDGE,"E2.4.3");Q167=makeQuery(id+"F0.imprint","IMPRINT",FACE,{"disambiguationData":[TD([[makeQuery(id+"F0.imprint","IMPRINT",EDGE,{"derivedFrom":subQ5}),-1.0]])]});}
            extrude(context, id + "F1", {"entities" : qUnion([Q0, Q1, Q2, Q3, Q4, Q5, Q6, Q7, Q8, Q9, Q10, Q11, Q12, Q13, Q14, Q15, Q16, Q17, Q18, Q19, Q20, Q21, Q22, Q23, Q24, Q25, Q26, Q27, Q28, Q29, Q30, Q31, Q32, Q33, Q34, Q35, Q36, Q37, Q38, Q39, Q40, Q41, Q42, Q43, Q44, Q45, Q46, Q47, Q48, Q49, Q50, Q51, Q52, Q53, Q54, Q55, Q56, Q57, Q58, Q59, Q60, Q61, Q62, Q63, Q64, Q65, Q66, Q67, Q68, Q69, Q70, Q71, Q72, Q73, Q74, Q75, Q76, Q77, Q78, Q79, Q80, Q81, Q82, Q83, Q84, Q85, Q86, Q87, Q88, Q89, Q90, Q91, Q92, Q93, Q94, Q95, Q96, Q97, Q98, Q99, Q100, Q101, Q102, Q103, Q104, Q105, Q106, Q107, Q108, Q109, Q110, Q111, Q112, Q113, Q114, Q115, Q116, Q117, Q118, Q119, Q120, Q121, Q122, Q123, Q124, Q125, Q126, Q127, Q128, Q129, Q130, Q131, Q132, Q133, Q134, Q135, Q136, Q137, Q138, Q139, Q140, Q141, Q142, Q143, Q144, Q145, Q146, Q147, Q148, Q149, Q150, Q151, Q152, Q153, Q154, Q155, Q156, Q157, Q158, Q159, Q160, Q161, Q162, Q163, Q164, Q165, Q166, Q167]), "depth" : 0.8 * mm});
        }
        {
            var Q0;
            {var subQ0=sQuery(id+"F0.wireOp",EDGE,"E1.right");var subQ1=sQuery(id+"F0.wireOp",EDGE,"E0");var subQ2=makeQuery(id+"F0.imprint","INTERSECT",VERTEX,{"derivedFrom":[subQ1,subQ0]});Q0=makeQuery(id+"F0.imprint","IMPRINT",FACE,{"disambiguationData":[TD([[makeQuery(id+"F0.imprint","IMPRINT",EDGE,{"disambiguationData":[TD([[subQ2,1.0]])],"derivedFrom":subQ1}),-1.0]])]});}
            var Q1;
            {var subQ0=sQuery(id+"F0.wireOp",EDGE,"E2.1.2");var subQ1=sQuery(id+"F0.wireOp",EDGE,"E0");var subQ2=makeQuery(id+"F0.imprint","INTERSECT",VERTEX,{"derivedFrom":[subQ1,subQ0]});Q1=makeQuery(id+"F0.imprint","IMPRINT",FACE,{"disambiguationData":[TD([[makeQuery(id+"F0.imprint","IMPRINT",EDGE,{"disambiguationData":[TD([[subQ2,-1.0]])],"derivedFrom":subQ1}),-1.0]])]});}
            var Q2;
            {var subQ0=sQuery(id+"F0.wireOp",EDGE,"E2.1.0");var subQ1=sQuery(id+"F0.wireOp",EDGE,"E0");var subQ2=makeQuery(id+"F0.imprint","INTERSECT",VERTEX,{"derivedFrom":[subQ1,subQ0]});Q2=makeQuery(id+"F0.imprint","IMPRINT",FACE,{"disambiguationData":[TD([[makeQuery(id+"F0.imprint","IMPRINT",EDGE,{"disambiguationData":[TD([[subQ2,-1.0]])],"derivedFrom":subQ1}),-1.0]])]});}
            var Q3;
            {var subQ0=sQuery(id+"F0.wireOp",EDGE,"E2.2.2");var subQ1=sQuery(id+"F0.wireOp",EDGE,"E0");var subQ2=makeQuery(id+"F0.imprint","INTERSECT",VERTEX,{"derivedFrom":[subQ1,subQ0]});Q3=makeQuery(id+"F0.imprint","IMPRINT",FACE,{"disambiguationData":[TD([[makeQuery(id+"F0.imprint","IMPRINT",EDGE,{"disambiguationData":[TD([[subQ2,-1.0]])],"derivedFrom":subQ1}),-1.0]])]});}
            var Q4;
            {var subQ0=sQuery(id+"F0.wireOp",EDGE,"E2.2.0");var subQ1=sQuery(id+"F0.wireOp",EDGE,"E0");var subQ2=makeQuery(id+"F0.imprint","INTERSECT",VERTEX,{"derivedFrom":[subQ1,subQ0]});Q4=makeQuery(id+"F0.imprint","IMPRINT",FACE,{"disambiguationData":[TD([[makeQuery(id+"F0.imprint","IMPRINT",EDGE,{"disambiguationData":[TD([[subQ2,-1.0]])],"derivedFrom":subQ1}),-1.0]])]});}
            var Q5;
            {var subQ0=sQuery(id+"F0.wireOp",EDGE,"E2.3.2");var subQ1=sQuery(id+"F0.wireOp",EDGE,"E0");var subQ2=makeQuery(id+"F0.imprint","INTERSECT",VERTEX,{"derivedFrom":[subQ1,subQ0]});Q5=makeQuery(id+"F0.imprint","IMPRINT",FACE,{"disambiguationData":[TD([[makeQuery(id+"F0.imprint","IMPRINT",EDGE,{"disambiguationData":[TD([[subQ2,-1.0]])],"derivedFrom":subQ1}),-1.0]])]});}
            var Q6;
            {var subQ0=sQuery(id+"F0.wireOp",EDGE,"E2.3.0");var subQ1=sQuery(id+"F0.wireOp",EDGE,"E0");var subQ2=makeQuery(id+"F0.imprint","INTERSECT",VERTEX,{"derivedFrom":[subQ1,subQ0]});Q6=makeQuery(id+"F0.imprint","IMPRINT",FACE,{"disambiguationData":[TD([[makeQuery(id+"F0.imprint","IMPRINT",EDGE,{"disambiguationData":[TD([[subQ2,-1.0]])],"derivedFrom":subQ1}),-1.0]])]});}
            var Q7;
            {var subQ0=sQuery(id+"F0.wireOp",EDGE,"E2.4.2");var subQ1=sQuery(id+"F0.wireOp",EDGE,"E0");var subQ2=makeQuery(id+"F0.imprint","INTERSECT",VERTEX,{"derivedFrom":[subQ1,subQ0]});Q7=makeQuery(id+"F0.imprint","IMPRINT",FACE,{"disambiguationData":[TD([[makeQuery(id+"F0.imprint","IMPRINT",EDGE,{"disambiguationData":[TD([[subQ2,-1.0]])],"derivedFrom":subQ1}),-1.0]])]});}
            var Q8;
            {var subQ0=sQuery(id+"F0.wireOp",EDGE,"E2.4.0");var subQ1=sQuery(id+"F0.wireOp",EDGE,"E0");var subQ2=makeQuery(id+"F0.imprint","INTERSECT",VERTEX,{"derivedFrom":[subQ1,subQ0]});Q8=makeQuery(id+"F0.imprint","IMPRINT",FACE,{"disambiguationData":[TD([[makeQuery(id+"F0.imprint","IMPRINT",EDGE,{"disambiguationData":[TD([[subQ2,-1.0]])],"derivedFrom":subQ1}),-1.0]])]});}
            var Q9;
            {var subQ0=sQuery(id+"F0.wireOp",EDGE,"E2.5.2");var subQ1=sQuery(id+"F0.wireOp",EDGE,"E0");var subQ2=makeQuery(id+"F0.imprint","INTERSECT",VERTEX,{"derivedFrom":[subQ1,subQ0]});Q9=makeQuery(id+"F0.imprint","IMPRINT",FACE,{"disambiguationData":[TD([[makeQuery(id+"F0.imprint","IMPRINT",EDGE,{"disambiguationData":[TD([[subQ2,-1.0]])],"derivedFrom":subQ1}),-1.0]])]});}
            var Q10;
            {var subQ0=sQuery(id+"F0.wireOp",EDGE,"E2.5.0");var subQ1=sQuery(id+"F0.wireOp",EDGE,"E0");var subQ2=makeQuery(id+"F0.imprint","INTERSECT",VERTEX,{"derivedFrom":[subQ1,subQ0]});Q10=makeQuery(id+"F0.imprint","IMPRINT",FACE,{"disambiguationData":[TD([[makeQuery(id+"F0.imprint","IMPRINT",EDGE,{"disambiguationData":[TD([[subQ2,-1.0]])],"derivedFrom":subQ1}),-1.0]])]});}
            var Q11;
            {var subQ0=sQuery(id+"F0.wireOp",EDGE,"E2.6.2");var subQ1=sQuery(id+"F0.wireOp",EDGE,"E0");var subQ2=makeQuery(id+"F0.imprint","INTERSECT",VERTEX,{"derivedFrom":[subQ1,subQ0]});Q11=makeQuery(id+"F0.imprint","IMPRINT",FACE,{"disambiguationData":[TD([[makeQuery(id+"F0.imprint","IMPRINT",EDGE,{"disambiguationData":[TD([[subQ2,-1.0]])],"derivedFrom":subQ1}),-1.0]])]});}
            var Q12;
            {var subQ0=sQuery(id+"F0.wireOp",EDGE,"E2.6.0");var subQ1=sQuery(id+"F0.wireOp",EDGE,"E0");var subQ2=makeQuery(id+"F0.imprint","INTERSECT",VERTEX,{"derivedFrom":[subQ1,subQ0]});Q12=makeQuery(id+"F0.imprint","IMPRINT",FACE,{"disambiguationData":[TD([[makeQuery(id+"F0.imprint","IMPRINT",EDGE,{"disambiguationData":[TD([[subQ2,-1.0]])],"derivedFrom":subQ1}),-1.0]])]});}
            var Q13;
            {var subQ0=sQuery(id+"F0.wireOp",EDGE,"E2.7.2");var subQ1=sQuery(id+"F0.wireOp",EDGE,"E0");var subQ2=makeQuery(id+"F0.imprint","INTERSECT",VERTEX,{"derivedFrom":[subQ1,subQ0]});Q13=makeQuery(id+"F0.imprint","IMPRINT",FACE,{"disambiguationData":[TD([[makeQuery(id+"F0.imprint","IMPRINT",EDGE,{"disambiguationData":[TD([[subQ2,-1.0]])],"derivedFrom":subQ1}),-1.0]])]});}
            var Q14;
            {var subQ0=sQuery(id+"F0.wireOp",EDGE,"E2.7.0");var subQ1=sQuery(id+"F0.wireOp",EDGE,"E0");var subQ2=makeQuery(id+"F0.imprint","INTERSECT",VERTEX,{"derivedFrom":[subQ1,subQ0]});Q14=makeQuery(id+"F0.imprint","IMPRINT",FACE,{"disambiguationData":[TD([[makeQuery(id+"F0.imprint","IMPRINT",EDGE,{"disambiguationData":[TD([[subQ2,-1.0]])],"derivedFrom":subQ1}),-1.0]])]});}
            var Q15;
            {var subQ0=sQuery(id+"F0.wireOp",EDGE,"E2.8.2");var subQ1=sQuery(id+"F0.wireOp",EDGE,"E0");var subQ2=makeQuery(id+"F0.imprint","INTERSECT",VERTEX,{"derivedFrom":[subQ1,subQ0]});Q15=makeQuery(id+"F0.imprint","IMPRINT",FACE,{"disambiguationData":[TD([[makeQuery(id+"F0.imprint","IMPRINT",EDGE,{"disambiguationData":[TD([[subQ2,-1.0]])],"derivedFrom":subQ1}),-1.0]])]});}
            var Q16;
            {var subQ0=sQuery(id+"F0.wireOp",EDGE,"E2.8.0");var subQ1=sQuery(id+"F0.wireOp",EDGE,"E0");var subQ2=makeQuery(id+"F0.imprint","INTERSECT",VERTEX,{"derivedFrom":[subQ1,subQ0]});Q16=makeQuery(id+"F0.imprint","IMPRINT",FACE,{"disambiguationData":[TD([[makeQuery(id+"F0.imprint","IMPRINT",EDGE,{"disambiguationData":[TD([[subQ2,-1.0]])],"derivedFrom":subQ1}),-1.0]])]});}
            var Q17;
            {var subQ0=sQuery(id+"F0.wireOp",EDGE,"E2.9.2");var subQ1=sQuery(id+"F0.wireOp",EDGE,"E0");var subQ2=makeQuery(id+"F0.imprint","INTERSECT",VERTEX,{"derivedFrom":[subQ1,subQ0]});Q17=makeQuery(id+"F0.imprint","IMPRINT",FACE,{"disambiguationData":[TD([[makeQuery(id+"F0.imprint","IMPRINT",EDGE,{"disambiguationData":[TD([[subQ2,-1.0]])],"derivedFrom":subQ1}),-1.0]])]});}
            var Q18;
            {var subQ0=sQuery(id+"F0.wireOp",EDGE,"E2.9.0");var subQ1=sQuery(id+"F0.wireOp",EDGE,"E0");var subQ2=makeQuery(id+"F0.imprint","INTERSECT",VERTEX,{"derivedFrom":[subQ1,subQ0]});Q18=makeQuery(id+"F0.imprint","IMPRINT",FACE,{"disambiguationData":[TD([[makeQuery(id+"F0.imprint","IMPRINT",EDGE,{"disambiguationData":[TD([[subQ2,-1.0]])],"derivedFrom":subQ1}),-1.0]])]});}
            var Q19;
            {var subQ0=sQuery(id+"F0.wireOp",EDGE,"E2.10.2");var subQ1=sQuery(id+"F0.wireOp",EDGE,"E0");var subQ2=makeQuery(id+"F0.imprint","INTERSECT",VERTEX,{"derivedFrom":[subQ1,subQ0]});Q19=makeQuery(id+"F0.imprint","IMPRINT",FACE,{"disambiguationData":[TD([[makeQuery(id+"F0.imprint","IMPRINT",EDGE,{"disambiguationData":[TD([[subQ2,-1.0]])],"derivedFrom":subQ1}),-1.0]])]});}
            var Q20;
            {var subQ0=sQuery(id+"F0.wireOp",EDGE,"E2.10.0");var subQ1=sQuery(id+"F0.wireOp",EDGE,"E0");var subQ2=makeQuery(id+"F0.imprint","INTERSECT",VERTEX,{"derivedFrom":[subQ1,subQ0]});Q20=makeQuery(id+"F0.imprint","IMPRINT",FACE,{"disambiguationData":[TD([[makeQuery(id+"F0.imprint","IMPRINT",EDGE,{"disambiguationData":[TD([[subQ2,-1.0]])],"derivedFrom":subQ1}),-1.0]])]});}
            var Q21;
            {var subQ0=sQuery(id+"F0.wireOp",EDGE,"E2.11.2");var subQ1=sQuery(id+"F0.wireOp",EDGE,"E0");var subQ2=makeQuery(id+"F0.imprint","INTERSECT",VERTEX,{"derivedFrom":[subQ1,subQ0]});Q21=makeQuery(id+"F0.imprint","IMPRINT",FACE,{"disambiguationData":[TD([[makeQuery(id+"F0.imprint","IMPRINT",EDGE,{"disambiguationData":[TD([[subQ2,-1.0]])],"derivedFrom":subQ1}),-1.0]])]});}
            var Q22;
            {var subQ0=sQuery(id+"F0.wireOp",EDGE,"E2.11.0");var subQ1=sQuery(id+"F0.wireOp",EDGE,"E0");var subQ2=makeQuery(id+"F0.imprint","INTERSECT",VERTEX,{"derivedFrom":[subQ1,subQ0]});Q22=makeQuery(id+"F0.imprint","IMPRINT",FACE,{"disambiguationData":[TD([[makeQuery(id+"F0.imprint","IMPRINT",EDGE,{"disambiguationData":[TD([[subQ2,-1.0]])],"derivedFrom":subQ1}),-1.0]])]});}
            var Q23;
            {var subQ0=sQuery(id+"F0.wireOp",EDGE,"E2.12.2");var subQ1=sQuery(id+"F0.wireOp",EDGE,"E0");var subQ2=makeQuery(id+"F0.imprint","INTERSECT",VERTEX,{"derivedFrom":[subQ1,subQ0]});Q23=makeQuery(id+"F0.imprint","IMPRINT",FACE,{"disambiguationData":[TD([[makeQuery(id+"F0.imprint","IMPRINT",EDGE,{"disambiguationData":[TD([[subQ2,-1.0]])],"derivedFrom":subQ1}),-1.0]])]});}
            var Q24;
            {var subQ0=sQuery(id+"F0.wireOp",EDGE,"E2.12.0");var subQ1=sQuery(id+"F0.wireOp",EDGE,"E0");var subQ2=makeQuery(id+"F0.imprint","INTERSECT",VERTEX,{"derivedFrom":[subQ1,subQ0]});Q24=makeQuery(id+"F0.imprint","IMPRINT",FACE,{"disambiguationData":[TD([[makeQuery(id+"F0.imprint","IMPRINT",EDGE,{"disambiguationData":[TD([[subQ2,-1.0]])],"derivedFrom":subQ1}),-1.0]])]});}
            var Q25;
            {var subQ0=sQuery(id+"F0.wireOp",EDGE,"E2.13.2");var subQ1=sQuery(id+"F0.wireOp",EDGE,"E0");var subQ2=makeQuery(id+"F0.imprint","INTERSECT",VERTEX,{"derivedFrom":[subQ1,subQ0]});Q25=makeQuery(id+"F0.imprint","IMPRINT",FACE,{"disambiguationData":[TD([[makeQuery(id+"F0.imprint","IMPRINT",EDGE,{"disambiguationData":[TD([[subQ2,-1.0]])],"derivedFrom":subQ1}),-1.0]])]});}
            var Q26;
            {var subQ0=sQuery(id+"F0.wireOp",EDGE,"E2.13.0");var subQ1=sQuery(id+"F0.wireOp",EDGE,"E0");var subQ2=makeQuery(id+"F0.imprint","INTERSECT",VERTEX,{"derivedFrom":[subQ1,subQ0]});Q26=makeQuery(id+"F0.imprint","IMPRINT",FACE,{"disambiguationData":[TD([[makeQuery(id+"F0.imprint","IMPRINT",EDGE,{"disambiguationData":[TD([[subQ2,-1.0]])],"derivedFrom":subQ1}),-1.0]])]});}
            var Q27;
            {var subQ0=sQuery(id+"F0.wireOp",EDGE,"E2.14.2");var subQ1=sQuery(id+"F0.wireOp",EDGE,"E0");var subQ2=makeQuery(id+"F0.imprint","INTERSECT",VERTEX,{"derivedFrom":[subQ1,subQ0]});Q27=makeQuery(id+"F0.imprint","IMPRINT",FACE,{"disambiguationData":[TD([[makeQuery(id+"F0.imprint","IMPRINT",EDGE,{"disambiguationData":[TD([[subQ2,-1.0]])],"derivedFrom":subQ1}),-1.0]])]});}
            var Q28;
            {var subQ0=sQuery(id+"F0.wireOp",EDGE,"E2.14.0");var subQ1=sQuery(id+"F0.wireOp",EDGE,"E0");var subQ2=makeQuery(id+"F0.imprint","INTERSECT",VERTEX,{"derivedFrom":[subQ1,subQ0]});Q28=makeQuery(id+"F0.imprint","IMPRINT",FACE,{"disambiguationData":[TD([[makeQuery(id+"F0.imprint","IMPRINT",EDGE,{"disambiguationData":[TD([[subQ2,-1.0]])],"derivedFrom":subQ1}),-1.0]])]});}
            var Q29;
            {var subQ0=sQuery(id+"F0.wireOp",EDGE,"E2.15.2");var subQ1=sQuery(id+"F0.wireOp",EDGE,"E0");var subQ2=makeQuery(id+"F0.imprint","INTERSECT",VERTEX,{"derivedFrom":[subQ1,subQ0]});Q29=makeQuery(id+"F0.imprint","IMPRINT",FACE,{"disambiguationData":[TD([[makeQuery(id+"F0.imprint","IMPRINT",EDGE,{"disambiguationData":[TD([[subQ2,-1.0]])],"derivedFrom":subQ1}),-1.0]])]});}
            var Q30;
            {var subQ0=sQuery(id+"F0.wireOp",EDGE,"E2.15.0");var subQ1=sQuery(id+"F0.wireOp",EDGE,"E0");var subQ2=makeQuery(id+"F0.imprint","INTERSECT",VERTEX,{"derivedFrom":[subQ1,subQ0]});Q30=makeQuery(id+"F0.imprint","IMPRINT",FACE,{"disambiguationData":[TD([[makeQuery(id+"F0.imprint","IMPRINT",EDGE,{"disambiguationData":[TD([[subQ2,-1.0]])],"derivedFrom":subQ1}),-1.0]])]});}
            var Q31;
            {var subQ0=sQuery(id+"F0.wireOp",EDGE,"E2.16.2");var subQ1=sQuery(id+"F0.wireOp",EDGE,"E0");var subQ2=makeQuery(id+"F0.imprint","INTERSECT",VERTEX,{"derivedFrom":[subQ1,subQ0]});Q31=makeQuery(id+"F0.imprint","IMPRINT",FACE,{"disambiguationData":[TD([[makeQuery(id+"F0.imprint","IMPRINT",EDGE,{"disambiguationData":[TD([[subQ2,-1.0]])],"derivedFrom":subQ1}),-1.0]])]});}
            var Q32;
            {var subQ0=sQuery(id+"F0.wireOp",EDGE,"E2.16.0");var subQ1=sQuery(id+"F0.wireOp",EDGE,"E0");var subQ2=makeQuery(id+"F0.imprint","INTERSECT",VERTEX,{"derivedFrom":[subQ1,subQ0]});Q32=makeQuery(id+"F0.imprint","IMPRINT",FACE,{"disambiguationData":[TD([[makeQuery(id+"F0.imprint","IMPRINT",EDGE,{"disambiguationData":[TD([[subQ2,-1.0]])],"derivedFrom":subQ1}),-1.0]])]});}
            var Q33;
            {var subQ0=sQuery(id+"F0.wireOp",EDGE,"E2.17.2");var subQ1=sQuery(id+"F0.wireOp",EDGE,"E0");var subQ2=makeQuery(id+"F0.imprint","INTERSECT",VERTEX,{"derivedFrom":[subQ1,subQ0]});Q33=makeQuery(id+"F0.imprint","IMPRINT",FACE,{"disambiguationData":[TD([[makeQuery(id+"F0.imprint","IMPRINT",EDGE,{"disambiguationData":[TD([[subQ2,-1.0]])],"derivedFrom":subQ1}),-1.0]])]});}
            var Q34;
            {var subQ0=sQuery(id+"F0.wireOp",EDGE,"E2.17.0");var subQ1=sQuery(id+"F0.wireOp",EDGE,"E0");var subQ2=makeQuery(id+"F0.imprint","INTERSECT",VERTEX,{"derivedFrom":[subQ1,subQ0]});Q34=makeQuery(id+"F0.imprint","IMPRINT",FACE,{"disambiguationData":[TD([[makeQuery(id+"F0.imprint","IMPRINT",EDGE,{"disambiguationData":[TD([[subQ2,-1.0]])],"derivedFrom":subQ1}),-1.0]])]});}
            var Q35;
            {var subQ0=sQuery(id+"F0.wireOp",EDGE,"E2.18.2");var subQ1=sQuery(id+"F0.wireOp",EDGE,"E0");var subQ2=makeQuery(id+"F0.imprint","INTERSECT",VERTEX,{"derivedFrom":[subQ1,subQ0]});Q35=makeQuery(id+"F0.imprint","IMPRINT",FACE,{"disambiguationData":[TD([[makeQuery(id+"F0.imprint","IMPRINT",EDGE,{"disambiguationData":[TD([[subQ2,-1.0]])],"derivedFrom":subQ1}),-1.0]])]});}
            var Q36;
            {var subQ0=sQuery(id+"F0.wireOp",EDGE,"E2.18.0");var subQ1=sQuery(id+"F0.wireOp",EDGE,"E0");var subQ2=makeQuery(id+"F0.imprint","INTERSECT",VERTEX,{"derivedFrom":[subQ1,subQ0]});Q36=makeQuery(id+"F0.imprint","IMPRINT",FACE,{"disambiguationData":[TD([[makeQuery(id+"F0.imprint","IMPRINT",EDGE,{"disambiguationData":[TD([[subQ2,-1.0]])],"derivedFrom":subQ1}),-1.0]])]});}
            var Q37;
            {var subQ0=sQuery(id+"F0.wireOp",EDGE,"E2.19.2");var subQ1=sQuery(id+"F0.wireOp",EDGE,"E0");var subQ2=makeQuery(id+"F0.imprint","INTERSECT",VERTEX,{"derivedFrom":[subQ1,subQ0]});Q37=makeQuery(id+"F0.imprint","IMPRINT",FACE,{"disambiguationData":[TD([[makeQuery(id+"F0.imprint","IMPRINT",EDGE,{"disambiguationData":[TD([[subQ2,-1.0]])],"derivedFrom":subQ1}),-1.0]])]});}
            var Q38;
            {var subQ0=sQuery(id+"F0.wireOp",EDGE,"E2.19.0");var subQ1=sQuery(id+"F0.wireOp",EDGE,"E0");var subQ2=makeQuery(id+"F0.imprint","INTERSECT",VERTEX,{"derivedFrom":[subQ1,subQ0]});Q38=makeQuery(id+"F0.imprint","IMPRINT",FACE,{"disambiguationData":[TD([[makeQuery(id+"F0.imprint","IMPRINT",EDGE,{"disambiguationData":[TD([[subQ2,-1.0]])],"derivedFrom":subQ1}),-1.0]])]});}
            var Q39;
            {var subQ0=sQuery(id+"F0.wireOp",EDGE,"E2.20.2");var subQ1=sQuery(id+"F0.wireOp",EDGE,"E0");var subQ2=makeQuery(id+"F0.imprint","INTERSECT",VERTEX,{"derivedFrom":[subQ1,subQ0]});Q39=makeQuery(id+"F0.imprint","IMPRINT",FACE,{"disambiguationData":[TD([[makeQuery(id+"F0.imprint","IMPRINT",EDGE,{"disambiguationData":[TD([[subQ2,-1.0]])],"derivedFrom":subQ1}),-1.0]])]});}
            var Q40;
            {var subQ0=sQuery(id+"F0.wireOp",EDGE,"E2.21.0");var subQ1=sQuery(id+"F0.wireOp",EDGE,"E0");var subQ2=makeQuery(id+"F0.imprint","INTERSECT",VERTEX,{"derivedFrom":[subQ1,subQ0]});Q40=makeQuery(id+"F0.imprint","IMPRINT",FACE,{"disambiguationData":[TD([[makeQuery(id+"F0.imprint","IMPRINT",EDGE,{"disambiguationData":[TD([[subQ2,-1.0]])],"derivedFrom":subQ1}),-1.0]])]});}
            var Q41;
            {var subQ0=sQuery(id+"F0.wireOp",EDGE,"E2.21.2");var subQ1=sQuery(id+"F0.wireOp",EDGE,"E0");var subQ2=makeQuery(id+"F0.imprint","INTERSECT",VERTEX,{"derivedFrom":[subQ1,subQ0]});Q41=makeQuery(id+"F0.imprint","IMPRINT",FACE,{"disambiguationData":[TD([[makeQuery(id+"F0.imprint","IMPRINT",EDGE,{"disambiguationData":[TD([[subQ2,-1.0]])],"derivedFrom":subQ1}),-1.0]])]});}
            var Q42;
            {var subQ0=sQuery(id+"F0.wireOp",EDGE,"E2.20.0");var subQ1=sQuery(id+"F0.wireOp",EDGE,"E0");var subQ2=makeQuery(id+"F0.imprint","INTERSECT",VERTEX,{"derivedFrom":[subQ1,subQ0]});Q42=makeQuery(id+"F0.imprint","IMPRINT",FACE,{"disambiguationData":[TD([[makeQuery(id+"F0.imprint","IMPRINT",EDGE,{"disambiguationData":[TD([[subQ2,-1.0]])],"derivedFrom":subQ1}),-1.0]])]});}
            var Q43;
            {var subQ0=sQuery(id+"F0.wireOp",EDGE,"E2.23.2");var subQ1=sQuery(id+"F0.wireOp",EDGE,"E0");var subQ2=makeQuery(id+"F0.imprint","INTERSECT",VERTEX,{"derivedFrom":[subQ1,subQ0]});Q43=makeQuery(id+"F0.imprint","IMPRINT",FACE,{"disambiguationData":[TD([[makeQuery(id+"F0.imprint","IMPRINT",EDGE,{"disambiguationData":[TD([[subQ2,-1.0]])],"derivedFrom":subQ1}),-1.0]])]});}
            var Q44;
            {var subQ0=sQuery(id+"F0.wireOp",EDGE,"E2.22.0");var subQ1=sQuery(id+"F0.wireOp",EDGE,"E0");var subQ2=makeQuery(id+"F0.imprint","INTERSECT",VERTEX,{"derivedFrom":[subQ1,subQ0]});Q44=makeQuery(id+"F0.imprint","IMPRINT",FACE,{"disambiguationData":[TD([[makeQuery(id+"F0.imprint","IMPRINT",EDGE,{"disambiguationData":[TD([[subQ2,-1.0]])],"derivedFrom":subQ1}),-1.0]])]});}
            var Q45;
            {var subQ0=sQuery(id+"F0.wireOp",EDGE,"E2.22.2");var subQ1=sQuery(id+"F0.wireOp",EDGE,"E0");var subQ2=makeQuery(id+"F0.imprint","INTERSECT",VERTEX,{"derivedFrom":[subQ1,subQ0]});Q45=makeQuery(id+"F0.imprint","IMPRINT",FACE,{"disambiguationData":[TD([[makeQuery(id+"F0.imprint","IMPRINT",EDGE,{"disambiguationData":[TD([[subQ2,-1.0]])],"derivedFrom":subQ1}),-1.0]])]});}
            var Q46;
            {var subQ0=sQuery(id+"F0.wireOp",EDGE,"E3.6.24.0");var subQ1=sQuery(id+"F0.wireOp",EDGE,"E0");var subQ2=makeQuery(id+"F0.imprint","INTERSECT",VERTEX,{"derivedFrom":[subQ1,subQ0]});Q46=makeQuery(id+"F0.imprint","IMPRINT",FACE,{"disambiguationData":[TD([[makeQuery(id+"F0.imprint","IMPRINT",EDGE,{"disambiguationData":[TD([[subQ2,-1.0]])],"derivedFrom":subQ1}),-1.0]])]});}
            var Q47;
            {var subQ0=sQuery(id+"F0.wireOp",EDGE,"E6");var subQ1=sQuery(id+"F0.wireOp",EDGE,"E2.23.0");var subQ2=makeQuery(id+"F0.imprint","INTERSECT",VERTEX,{"derivedFrom":[subQ1,subQ0]});Q47=makeQuery(id+"F0.imprint","IMPRINT",FACE,{"disambiguationData":[TD([[makeQuery(id+"F0.imprint","IMPRINT",EDGE,{"disambiguationData":[TD([[subQ2,1.0]])],"derivedFrom":subQ1}),-1.0]])]});}
            var Q48;
            {var subQ0=sQuery(id+"F0.wireOp",EDGE,"E2.23.0");var subQ1=sQuery(id+"F0.wireOp",EDGE,"E0");var subQ2=makeQuery(id+"F0.imprint","INTERSECT",VERTEX,{"derivedFrom":[subQ1,subQ0]});Q48=makeQuery(id+"F0.imprint","IMPRINT",FACE,{"disambiguationData":[TD([[makeQuery(id+"F0.imprint","IMPRINT",EDGE,{"disambiguationData":[TD([[subQ2,-1.0]])],"derivedFrom":subQ1}),-1.0]])]});}
            var Q49;
            {var subQ0=sQuery(id+"F0.wireOp",EDGE,"E6");var subQ1=sQuery(id+"F0.wireOp",EDGE,"E2.23.0");var subQ2=makeQuery(id+"F0.imprint","INTERSECT",VERTEX,{"derivedFrom":[subQ1,subQ0]});Q49=makeQuery(id+"F0.imprint","IMPRINT",FACE,{"disambiguationData":[TD([[makeQuery(id+"F0.imprint","IMPRINT",EDGE,{"disambiguationData":[TD([[subQ2,1.0]])],"derivedFrom":subQ1}),1.0]])]});}
            var Q50;
            {var subQ0=sQuery(id+"F0.wireOp",EDGE,"E6");var subQ1=sQuery(id+"F0.wireOp",EDGE,"E2.22.0");var subQ2=makeQuery(id+"F0.imprint","INTERSECT",VERTEX,{"derivedFrom":[subQ1,subQ0]});Q50=makeQuery(id+"F0.imprint","IMPRINT",FACE,{"disambiguationData":[TD([[makeQuery(id+"F0.imprint","IMPRINT",EDGE,{"disambiguationData":[TD([[subQ2,1.0]])],"derivedFrom":subQ1}),-1.0]])]});}
            var Q51;
            {var subQ0=sQuery(id+"F0.wireOp",EDGE,"E6");var subQ1=sQuery(id+"F0.wireOp",EDGE,"E2.22.0");var subQ2=makeQuery(id+"F0.imprint","INTERSECT",VERTEX,{"derivedFrom":[subQ1,subQ0]});Q51=makeQuery(id+"F0.imprint","IMPRINT",FACE,{"disambiguationData":[TD([[makeQuery(id+"F0.imprint","IMPRINT",EDGE,{"disambiguationData":[TD([[subQ2,1.0]])],"derivedFrom":subQ1}),1.0]])]});}
            var Q52;
            {var subQ0=sQuery(id+"F0.wireOp",EDGE,"E6");var subQ1=sQuery(id+"F0.wireOp",EDGE,"E2.21.0");var subQ2=makeQuery(id+"F0.imprint","INTERSECT",VERTEX,{"derivedFrom":[subQ1,subQ0]});Q52=makeQuery(id+"F0.imprint","IMPRINT",FACE,{"disambiguationData":[TD([[makeQuery(id+"F0.imprint","IMPRINT",EDGE,{"disambiguationData":[TD([[subQ2,1.0]])],"derivedFrom":subQ1}),-1.0]])]});}
            var Q53;
            {var subQ0=sQuery(id+"F0.wireOp",EDGE,"E6");var subQ1=sQuery(id+"F0.wireOp",EDGE,"E2.20.0");var subQ2=makeQuery(id+"F0.imprint","INTERSECT",VERTEX,{"derivedFrom":[subQ1,subQ0]});Q53=makeQuery(id+"F0.imprint","IMPRINT",FACE,{"disambiguationData":[TD([[makeQuery(id+"F0.imprint","IMPRINT",EDGE,{"disambiguationData":[TD([[subQ2,1.0]])],"derivedFrom":subQ1}),-1.0]])]});}
            var Q54;
            {var subQ0=sQuery(id+"F0.wireOp",EDGE,"E6");var subQ1=sQuery(id+"F0.wireOp",EDGE,"E2.20.0");var subQ2=makeQuery(id+"F0.imprint","INTERSECT",VERTEX,{"derivedFrom":[subQ1,subQ0]});Q54=makeQuery(id+"F0.imprint","IMPRINT",FACE,{"disambiguationData":[TD([[makeQuery(id+"F0.imprint","IMPRINT",EDGE,{"disambiguationData":[TD([[subQ2,1.0]])],"derivedFrom":subQ1}),1.0]])]});}
            var Q55;
            {var subQ0=sQuery(id+"F0.wireOp",EDGE,"E6");var subQ1=sQuery(id+"F0.wireOp",EDGE,"E2.21.0");var subQ2=makeQuery(id+"F0.imprint","INTERSECT",VERTEX,{"derivedFrom":[subQ1,subQ0]});Q55=makeQuery(id+"F0.imprint","IMPRINT",FACE,{"disambiguationData":[TD([[makeQuery(id+"F0.imprint","IMPRINT",EDGE,{"disambiguationData":[TD([[subQ2,1.0]])],"derivedFrom":subQ1}),1.0]])]});}
            var Q56;
            {var subQ0=sQuery(id+"F0.wireOp",EDGE,"E6");var subQ1=sQuery(id+"F0.wireOp",EDGE,"E2.19.0");var subQ2=makeQuery(id+"F0.imprint","INTERSECT",VERTEX,{"derivedFrom":[subQ1,subQ0]});Q56=makeQuery(id+"F0.imprint","IMPRINT",FACE,{"disambiguationData":[TD([[makeQuery(id+"F0.imprint","IMPRINT",EDGE,{"disambiguationData":[TD([[subQ2,1.0]])],"derivedFrom":subQ1}),-1.0]])]});}
            var Q57;
            {var subQ0=sQuery(id+"F0.wireOp",EDGE,"E6");var subQ1=sQuery(id+"F0.wireOp",EDGE,"E2.19.0");var subQ2=makeQuery(id+"F0.imprint","INTERSECT",VERTEX,{"derivedFrom":[subQ1,subQ0]});Q57=makeQuery(id+"F0.imprint","IMPRINT",FACE,{"disambiguationData":[TD([[makeQuery(id+"F0.imprint","IMPRINT",EDGE,{"disambiguationData":[TD([[subQ2,1.0]])],"derivedFrom":subQ1}),1.0]])]});}
            var Q58;
            {var subQ0=sQuery(id+"F0.wireOp",EDGE,"E6");var subQ1=sQuery(id+"F0.wireOp",EDGE,"E2.18.0");var subQ2=makeQuery(id+"F0.imprint","INTERSECT",VERTEX,{"derivedFrom":[subQ1,subQ0]});Q58=makeQuery(id+"F0.imprint","IMPRINT",FACE,{"disambiguationData":[TD([[makeQuery(id+"F0.imprint","IMPRINT",EDGE,{"disambiguationData":[TD([[subQ2,1.0]])],"derivedFrom":subQ1}),-1.0]])]});}
            var Q59;
            {var subQ0=sQuery(id+"F0.wireOp",EDGE,"E6");var subQ1=sQuery(id+"F0.wireOp",EDGE,"E2.18.0");var subQ2=makeQuery(id+"F0.imprint","INTERSECT",VERTEX,{"derivedFrom":[subQ1,subQ0]});Q59=makeQuery(id+"F0.imprint","IMPRINT",FACE,{"disambiguationData":[TD([[makeQuery(id+"F0.imprint","IMPRINT",EDGE,{"disambiguationData":[TD([[subQ2,1.0]])],"derivedFrom":subQ1}),1.0]])]});}
            var Q60;
            {var subQ0=sQuery(id+"F0.wireOp",EDGE,"E6");var subQ1=sQuery(id+"F0.wireOp",EDGE,"E2.17.0");var subQ2=makeQuery(id+"F0.imprint","INTERSECT",VERTEX,{"derivedFrom":[subQ1,subQ0]});Q60=makeQuery(id+"F0.imprint","IMPRINT",FACE,{"disambiguationData":[TD([[makeQuery(id+"F0.imprint","IMPRINT",EDGE,{"disambiguationData":[TD([[subQ2,1.0]])],"derivedFrom":subQ1}),-1.0]])]});}
            var Q61;
            {var subQ0=sQuery(id+"F0.wireOp",EDGE,"E6");var subQ1=sQuery(id+"F0.wireOp",EDGE,"E2.17.0");var subQ2=makeQuery(id+"F0.imprint","INTERSECT",VERTEX,{"derivedFrom":[subQ1,subQ0]});Q61=makeQuery(id+"F0.imprint","IMPRINT",FACE,{"disambiguationData":[TD([[makeQuery(id+"F0.imprint","IMPRINT",EDGE,{"disambiguationData":[TD([[subQ2,1.0]])],"derivedFrom":subQ1}),1.0]])]});}
            var Q62;
            {var subQ0=sQuery(id+"F0.wireOp",EDGE,"E6");var subQ1=sQuery(id+"F0.wireOp",EDGE,"E2.16.0");var subQ2=makeQuery(id+"F0.imprint","INTERSECT",VERTEX,{"derivedFrom":[subQ1,subQ0]});Q62=makeQuery(id+"F0.imprint","IMPRINT",FACE,{"disambiguationData":[TD([[makeQuery(id+"F0.imprint","IMPRINT",EDGE,{"disambiguationData":[TD([[subQ2,1.0]])],"derivedFrom":subQ1}),-1.0]])]});}
            var Q63;
            {var subQ0=sQuery(id+"F0.wireOp",EDGE,"E6");var subQ1=sQuery(id+"F0.wireOp",EDGE,"E2.16.0");var subQ2=makeQuery(id+"F0.imprint","INTERSECT",VERTEX,{"derivedFrom":[subQ1,subQ0]});Q63=makeQuery(id+"F0.imprint","IMPRINT",FACE,{"disambiguationData":[TD([[makeQuery(id+"F0.imprint","IMPRINT",EDGE,{"disambiguationData":[TD([[subQ2,1.0]])],"derivedFrom":subQ1}),1.0]])]});}
            var Q64;
            {var subQ0=sQuery(id+"F0.wireOp",EDGE,"E6");var subQ1=sQuery(id+"F0.wireOp",EDGE,"E2.15.0");var subQ2=makeQuery(id+"F0.imprint","INTERSECT",VERTEX,{"derivedFrom":[subQ1,subQ0]});Q64=makeQuery(id+"F0.imprint","IMPRINT",FACE,{"disambiguationData":[TD([[makeQuery(id+"F0.imprint","IMPRINT",EDGE,{"disambiguationData":[TD([[subQ2,1.0]])],"derivedFrom":subQ1}),-1.0]])]});}
            var Q65;
            {var subQ0=sQuery(id+"F0.wireOp",EDGE,"E6");var subQ1=sQuery(id+"F0.wireOp",EDGE,"E2.15.0");var subQ2=makeQuery(id+"F0.imprint","INTERSECT",VERTEX,{"derivedFrom":[subQ1,subQ0]});Q65=makeQuery(id+"F0.imprint","IMPRINT",FACE,{"disambiguationData":[TD([[makeQuery(id+"F0.imprint","IMPRINT",EDGE,{"disambiguationData":[TD([[subQ2,1.0]])],"derivedFrom":subQ1}),1.0]])]});}
            var Q66;
            {var subQ0=sQuery(id+"F0.wireOp",EDGE,"E6");var subQ1=sQuery(id+"F0.wireOp",EDGE,"E2.14.0");var subQ2=makeQuery(id+"F0.imprint","INTERSECT",VERTEX,{"derivedFrom":[subQ1,subQ0]});Q66=makeQuery(id+"F0.imprint","IMPRINT",FACE,{"disambiguationData":[TD([[makeQuery(id+"F0.imprint","IMPRINT",EDGE,{"disambiguationData":[TD([[subQ2,1.0]])],"derivedFrom":subQ1}),-1.0]])]});}
            var Q67;
            {var subQ0=sQuery(id+"F0.wireOp",EDGE,"E6");var subQ1=sQuery(id+"F0.wireOp",EDGE,"E2.14.0");var subQ2=makeQuery(id+"F0.imprint","INTERSECT",VERTEX,{"derivedFrom":[subQ1,subQ0]});Q67=makeQuery(id+"F0.imprint","IMPRINT",FACE,{"disambiguationData":[TD([[makeQuery(id+"F0.imprint","IMPRINT",EDGE,{"disambiguationData":[TD([[subQ2,1.0]])],"derivedFrom":subQ1}),1.0]])]});}
            var Q68;
            {var subQ0=sQuery(id+"F0.wireOp",EDGE,"E6");var subQ1=sQuery(id+"F0.wireOp",EDGE,"E2.13.0");var subQ2=makeQuery(id+"F0.imprint","INTERSECT",VERTEX,{"derivedFrom":[subQ1,subQ0]});Q68=makeQuery(id+"F0.imprint","IMPRINT",FACE,{"disambiguationData":[TD([[makeQuery(id+"F0.imprint","IMPRINT",EDGE,{"disambiguationData":[TD([[subQ2,1.0]])],"derivedFrom":subQ1}),-1.0]])]});}
            var Q69;
            {var subQ0=sQuery(id+"F0.wireOp",EDGE,"E6");var subQ1=sQuery(id+"F0.wireOp",EDGE,"E2.13.0");var subQ2=makeQuery(id+"F0.imprint","INTERSECT",VERTEX,{"derivedFrom":[subQ1,subQ0]});Q69=makeQuery(id+"F0.imprint","IMPRINT",FACE,{"disambiguationData":[TD([[makeQuery(id+"F0.imprint","IMPRINT",EDGE,{"disambiguationData":[TD([[subQ2,1.0]])],"derivedFrom":subQ1}),1.0]])]});}
            var Q70;
            {var subQ0=sQuery(id+"F0.wireOp",EDGE,"E6");var subQ1=sQuery(id+"F0.wireOp",EDGE,"E2.12.0");var subQ2=makeQuery(id+"F0.imprint","INTERSECT",VERTEX,{"derivedFrom":[subQ1,subQ0]});Q70=makeQuery(id+"F0.imprint","IMPRINT",FACE,{"disambiguationData":[TD([[makeQuery(id+"F0.imprint","IMPRINT",EDGE,{"disambiguationData":[TD([[subQ2,1.0]])],"derivedFrom":subQ1}),-1.0]])]});}
            var Q71;
            {var subQ0=sQuery(id+"F0.wireOp",EDGE,"E6");var subQ1=sQuery(id+"F0.wireOp",EDGE,"E2.12.0");var subQ2=makeQuery(id+"F0.imprint","INTERSECT",VERTEX,{"derivedFrom":[subQ1,subQ0]});Q71=makeQuery(id+"F0.imprint","IMPRINT",FACE,{"disambiguationData":[TD([[makeQuery(id+"F0.imprint","IMPRINT",EDGE,{"disambiguationData":[TD([[subQ2,1.0]])],"derivedFrom":subQ1}),1.0]])]});}
            var Q72;
            {var subQ0=sQuery(id+"F0.wireOp",EDGE,"E6");var subQ1=sQuery(id+"F0.wireOp",EDGE,"E2.11.0");var subQ2=makeQuery(id+"F0.imprint","INTERSECT",VERTEX,{"derivedFrom":[subQ1,subQ0]});Q72=makeQuery(id+"F0.imprint","IMPRINT",FACE,{"disambiguationData":[TD([[makeQuery(id+"F0.imprint","IMPRINT",EDGE,{"disambiguationData":[TD([[subQ2,1.0]])],"derivedFrom":subQ1}),-1.0]])]});}
            var Q73;
            {var subQ0=sQuery(id+"F0.wireOp",EDGE,"E6");var subQ1=sQuery(id+"F0.wireOp",EDGE,"E2.11.0");var subQ2=makeQuery(id+"F0.imprint","INTERSECT",VERTEX,{"derivedFrom":[subQ1,subQ0]});Q73=makeQuery(id+"F0.imprint","IMPRINT",FACE,{"disambiguationData":[TD([[makeQuery(id+"F0.imprint","IMPRINT",EDGE,{"disambiguationData":[TD([[subQ2,1.0]])],"derivedFrom":subQ1}),1.0]])]});}
            var Q74;
            {var subQ0=sQuery(id+"F0.wireOp",EDGE,"E6");var subQ1=sQuery(id+"F0.wireOp",EDGE,"E2.10.0");var subQ2=makeQuery(id+"F0.imprint","INTERSECT",VERTEX,{"derivedFrom":[subQ1,subQ0]});Q74=makeQuery(id+"F0.imprint","IMPRINT",FACE,{"disambiguationData":[TD([[makeQuery(id+"F0.imprint","IMPRINT",EDGE,{"disambiguationData":[TD([[subQ2,1.0]])],"derivedFrom":subQ1}),1.0]])]});}
            var Q75;
            {var subQ0=sQuery(id+"F0.wireOp",EDGE,"E6");var subQ1=sQuery(id+"F0.wireOp",EDGE,"E2.10.0");var subQ2=makeQuery(id+"F0.imprint","INTERSECT",VERTEX,{"derivedFrom":[subQ1,subQ0]});Q75=makeQuery(id+"F0.imprint","IMPRINT",FACE,{"disambiguationData":[TD([[makeQuery(id+"F0.imprint","IMPRINT",EDGE,{"disambiguationData":[TD([[subQ2,1.0]])],"derivedFrom":subQ1}),-1.0]])]});}
            var Q76;
            {var subQ0=sQuery(id+"F0.wireOp",EDGE,"E6");var subQ1=sQuery(id+"F0.wireOp",EDGE,"E2.9.0");var subQ2=makeQuery(id+"F0.imprint","INTERSECT",VERTEX,{"derivedFrom":[subQ1,subQ0]});Q76=makeQuery(id+"F0.imprint","IMPRINT",FACE,{"disambiguationData":[TD([[makeQuery(id+"F0.imprint","IMPRINT",EDGE,{"disambiguationData":[TD([[subQ2,1.0]])],"derivedFrom":subQ1}),-1.0]])]});}
            var Q77;
            {var subQ0=sQuery(id+"F0.wireOp",EDGE,"E6");var subQ1=sQuery(id+"F0.wireOp",EDGE,"E2.9.0");var subQ2=makeQuery(id+"F0.imprint","INTERSECT",VERTEX,{"derivedFrom":[subQ1,subQ0]});Q77=makeQuery(id+"F0.imprint","IMPRINT",FACE,{"disambiguationData":[TD([[makeQuery(id+"F0.imprint","IMPRINT",EDGE,{"disambiguationData":[TD([[subQ2,1.0]])],"derivedFrom":subQ1}),1.0]])]});}
            var Q78;
            {var subQ0=sQuery(id+"F0.wireOp",EDGE,"E6");var subQ1=sQuery(id+"F0.wireOp",EDGE,"E2.8.0");var subQ2=makeQuery(id+"F0.imprint","INTERSECT",VERTEX,{"derivedFrom":[subQ1,subQ0]});Q78=makeQuery(id+"F0.imprint","IMPRINT",FACE,{"disambiguationData":[TD([[makeQuery(id+"F0.imprint","IMPRINT",EDGE,{"disambiguationData":[TD([[subQ2,1.0]])],"derivedFrom":subQ1}),-1.0]])]});}
            var Q79;
            {var subQ0=sQuery(id+"F0.wireOp",EDGE,"E6");var subQ1=sQuery(id+"F0.wireOp",EDGE,"E2.8.0");var subQ2=makeQuery(id+"F0.imprint","INTERSECT",VERTEX,{"derivedFrom":[subQ1,subQ0]});Q79=makeQuery(id+"F0.imprint","IMPRINT",FACE,{"disambiguationData":[TD([[makeQuery(id+"F0.imprint","IMPRINT",EDGE,{"disambiguationData":[TD([[subQ2,1.0]])],"derivedFrom":subQ1}),1.0]])]});}
            var Q80;
            {var subQ0=sQuery(id+"F0.wireOp",EDGE,"E6");var subQ1=sQuery(id+"F0.wireOp",EDGE,"E2.7.0");var subQ2=makeQuery(id+"F0.imprint","INTERSECT",VERTEX,{"derivedFrom":[subQ1,subQ0]});Q80=makeQuery(id+"F0.imprint","IMPRINT",FACE,{"disambiguationData":[TD([[makeQuery(id+"F0.imprint","IMPRINT",EDGE,{"disambiguationData":[TD([[subQ2,1.0]])],"derivedFrom":subQ1}),-1.0]])]});}
            var Q81;
            {var subQ0=sQuery(id+"F0.wireOp",EDGE,"E6");var subQ1=sQuery(id+"F0.wireOp",EDGE,"E2.7.0");var subQ2=makeQuery(id+"F0.imprint","INTERSECT",VERTEX,{"derivedFrom":[subQ1,subQ0]});Q81=makeQuery(id+"F0.imprint","IMPRINT",FACE,{"disambiguationData":[TD([[makeQuery(id+"F0.imprint","IMPRINT",EDGE,{"disambiguationData":[TD([[subQ2,1.0]])],"derivedFrom":subQ1}),1.0]])]});}
            var Q82;
            {var subQ0=sQuery(id+"F0.wireOp",EDGE,"E6");var subQ1=sQuery(id+"F0.wireOp",EDGE,"E2.6.0");var subQ2=makeQuery(id+"F0.imprint","INTERSECT",VERTEX,{"derivedFrom":[subQ1,subQ0]});Q82=makeQuery(id+"F0.imprint","IMPRINT",FACE,{"disambiguationData":[TD([[makeQuery(id+"F0.imprint","IMPRINT",EDGE,{"disambiguationData":[TD([[subQ2,1.0]])],"derivedFrom":subQ1}),-1.0]])]});}
            var Q83;
            {var subQ0=sQuery(id+"F0.wireOp",EDGE,"E6");var subQ1=sQuery(id+"F0.wireOp",EDGE,"E2.6.0");var subQ2=makeQuery(id+"F0.imprint","INTERSECT",VERTEX,{"derivedFrom":[subQ1,subQ0]});Q83=makeQuery(id+"F0.imprint","IMPRINT",FACE,{"disambiguationData":[TD([[makeQuery(id+"F0.imprint","IMPRINT",EDGE,{"disambiguationData":[TD([[subQ2,1.0]])],"derivedFrom":subQ1}),1.0]])]});}
            var Q84;
            {var subQ0=sQuery(id+"F0.wireOp",EDGE,"E6");var subQ1=sQuery(id+"F0.wireOp",EDGE,"E2.5.0");var subQ2=makeQuery(id+"F0.imprint","INTERSECT",VERTEX,{"derivedFrom":[subQ1,subQ0]});Q84=makeQuery(id+"F0.imprint","IMPRINT",FACE,{"disambiguationData":[TD([[makeQuery(id+"F0.imprint","IMPRINT",EDGE,{"disambiguationData":[TD([[subQ2,1.0]])],"derivedFrom":subQ1}),-1.0]])]});}
            var Q85;
            {var subQ0=sQuery(id+"F0.wireOp",EDGE,"E6");var subQ1=sQuery(id+"F0.wireOp",EDGE,"E2.5.0");var subQ2=makeQuery(id+"F0.imprint","INTERSECT",VERTEX,{"derivedFrom":[subQ1,subQ0]});Q85=makeQuery(id+"F0.imprint","IMPRINT",FACE,{"disambiguationData":[TD([[makeQuery(id+"F0.imprint","IMPRINT",EDGE,{"disambiguationData":[TD([[subQ2,1.0]])],"derivedFrom":subQ1}),1.0]])]});}
            var Q86;
            {var subQ0=sQuery(id+"F0.wireOp",EDGE,"E6");var subQ1=sQuery(id+"F0.wireOp",EDGE,"E2.4.0");var subQ2=makeQuery(id+"F0.imprint","INTERSECT",VERTEX,{"derivedFrom":[subQ1,subQ0]});Q86=makeQuery(id+"F0.imprint","IMPRINT",FACE,{"disambiguationData":[TD([[makeQuery(id+"F0.imprint","IMPRINT",EDGE,{"disambiguationData":[TD([[subQ2,1.0]])],"derivedFrom":subQ1}),-1.0]])]});}
            var Q87;
            {var subQ0=sQuery(id+"F0.wireOp",EDGE,"E6");var subQ1=sQuery(id+"F0.wireOp",EDGE,"E2.4.0");var subQ2=makeQuery(id+"F0.imprint","INTERSECT",VERTEX,{"derivedFrom":[subQ1,subQ0]});Q87=makeQuery(id+"F0.imprint","IMPRINT",FACE,{"disambiguationData":[TD([[makeQuery(id+"F0.imprint","IMPRINT",EDGE,{"disambiguationData":[TD([[subQ2,1.0]])],"derivedFrom":subQ1}),1.0]])]});}
            var Q88;
            {var subQ0=sQuery(id+"F0.wireOp",EDGE,"E6");var subQ1=sQuery(id+"F0.wireOp",EDGE,"E2.3.0");var subQ2=makeQuery(id+"F0.imprint","INTERSECT",VERTEX,{"derivedFrom":[subQ1,subQ0]});Q88=makeQuery(id+"F0.imprint","IMPRINT",FACE,{"disambiguationData":[TD([[makeQuery(id+"F0.imprint","IMPRINT",EDGE,{"disambiguationData":[TD([[subQ2,1.0]])],"derivedFrom":subQ1}),-1.0]])]});}
            var Q89;
            {var subQ0=sQuery(id+"F0.wireOp",EDGE,"E6");var subQ1=sQuery(id+"F0.wireOp",EDGE,"E2.3.0");var subQ2=makeQuery(id+"F0.imprint","INTERSECT",VERTEX,{"derivedFrom":[subQ1,subQ0]});Q89=makeQuery(id+"F0.imprint","IMPRINT",FACE,{"disambiguationData":[TD([[makeQuery(id+"F0.imprint","IMPRINT",EDGE,{"disambiguationData":[TD([[subQ2,1.0]])],"derivedFrom":subQ1}),1.0]])]});}
            var Q90;
            {var subQ0=sQuery(id+"F0.wireOp",EDGE,"E6");var subQ1=sQuery(id+"F0.wireOp",EDGE,"E2.2.0");var subQ2=makeQuery(id+"F0.imprint","INTERSECT",VERTEX,{"derivedFrom":[subQ1,subQ0]});Q90=makeQuery(id+"F0.imprint","IMPRINT",FACE,{"disambiguationData":[TD([[makeQuery(id+"F0.imprint","IMPRINT",EDGE,{"disambiguationData":[TD([[subQ2,1.0]])],"derivedFrom":subQ1}),-1.0]])]});}
            var Q91;
            {var subQ0=sQuery(id+"F0.wireOp",EDGE,"E6");var subQ1=sQuery(id+"F0.wireOp",EDGE,"E2.2.0");var subQ2=makeQuery(id+"F0.imprint","INTERSECT",VERTEX,{"derivedFrom":[subQ1,subQ0]});Q91=makeQuery(id+"F0.imprint","IMPRINT",FACE,{"disambiguationData":[TD([[makeQuery(id+"F0.imprint","IMPRINT",EDGE,{"disambiguationData":[TD([[subQ2,1.0]])],"derivedFrom":subQ1}),1.0]])]});}
            var Q92;
            {var subQ0=sQuery(id+"F0.wireOp",EDGE,"E6");var subQ1=sQuery(id+"F0.wireOp",EDGE,"E2.1.0");var subQ2=makeQuery(id+"F0.imprint","INTERSECT",VERTEX,{"derivedFrom":[subQ1,subQ0]});Q92=makeQuery(id+"F0.imprint","IMPRINT",FACE,{"disambiguationData":[TD([[makeQuery(id+"F0.imprint","IMPRINT",EDGE,{"disambiguationData":[TD([[subQ2,1.0]])],"derivedFrom":subQ1}),-1.0]])]});}
            var Q93;
            {var subQ0=sQuery(id+"F0.wireOp",EDGE,"E6");var subQ1=sQuery(id+"F0.wireOp",EDGE,"E2.1.0");var subQ2=makeQuery(id+"F0.imprint","INTERSECT",VERTEX,{"derivedFrom":[subQ1,subQ0]});Q93=makeQuery(id+"F0.imprint","IMPRINT",FACE,{"disambiguationData":[TD([[makeQuery(id+"F0.imprint","IMPRINT",EDGE,{"disambiguationData":[TD([[subQ2,1.0]])],"derivedFrom":subQ1}),1.0]])]});}
            var Q94;
            {var subQ0=sQuery(id+"F0.wireOp",EDGE,"E6");var subQ1=sQuery(id+"F0.wireOp",EDGE,"E1.left");var subQ2=makeQuery(id+"F0.imprint","INTERSECT",VERTEX,{"derivedFrom":[subQ1,subQ0]});Q94=makeQuery(id+"F0.imprint","IMPRINT",FACE,{"disambiguationData":[TD([[makeQuery(id+"F0.imprint","IMPRINT",EDGE,{"disambiguationData":[TD([[subQ2,1.0]])],"derivedFrom":subQ1}),-1.0]])]});}
            var Q95;
            {var subQ0=sQuery(id+"F0.wireOp",EDGE,"E6");var subQ1=sQuery(id+"F0.wireOp",EDGE,"E1.left");var subQ2=makeQuery(id+"F0.imprint","INTERSECT",VERTEX,{"derivedFrom":[subQ1,subQ0]});Q95=makeQuery(id+"F0.imprint","IMPRINT",FACE,{"disambiguationData":[TD([[makeQuery(id+"F0.imprint","IMPRINT",EDGE,{"disambiguationData":[TD([[subQ2,1.0]])],"derivedFrom":subQ1}),1.0]])]});}
            extrude(context, id + "F2", {"entities" : qUnion([Q0, Q1, Q2, Q3, Q4, Q5, Q6, Q7, Q8, Q9, Q10, Q11, Q12, Q13, Q14, Q15, Q16, Q17, Q18, Q19, Q20, Q21, Q22, Q23, Q24, Q25, Q26, Q27, Q28, Q29, Q30, Q31, Q32, Q33, Q34, Q35, Q36, Q37, Q38, Q39, Q40, Q41, Q42, Q43, Q44, Q45, Q46, Q47, Q48, Q49, Q50, Q51, Q52, Q53, Q54, Q55, Q56, Q57, Q58, Q59, Q60, Q61, Q62, Q63, Q64, Q65, Q66, Q67, Q68, Q69, Q70, Q71, Q72, Q73, Q74, Q75, Q76, Q77, Q78, Q79, Q80, Q81, Q82, Q83, Q84, Q85, Q86, Q87, Q88, Q89, Q90, Q91, Q92, Q93, Q94, Q95]), "operationType" : NewBodyOperationType.ADD, "depth" : 1.4 * mm});
        }
    });
